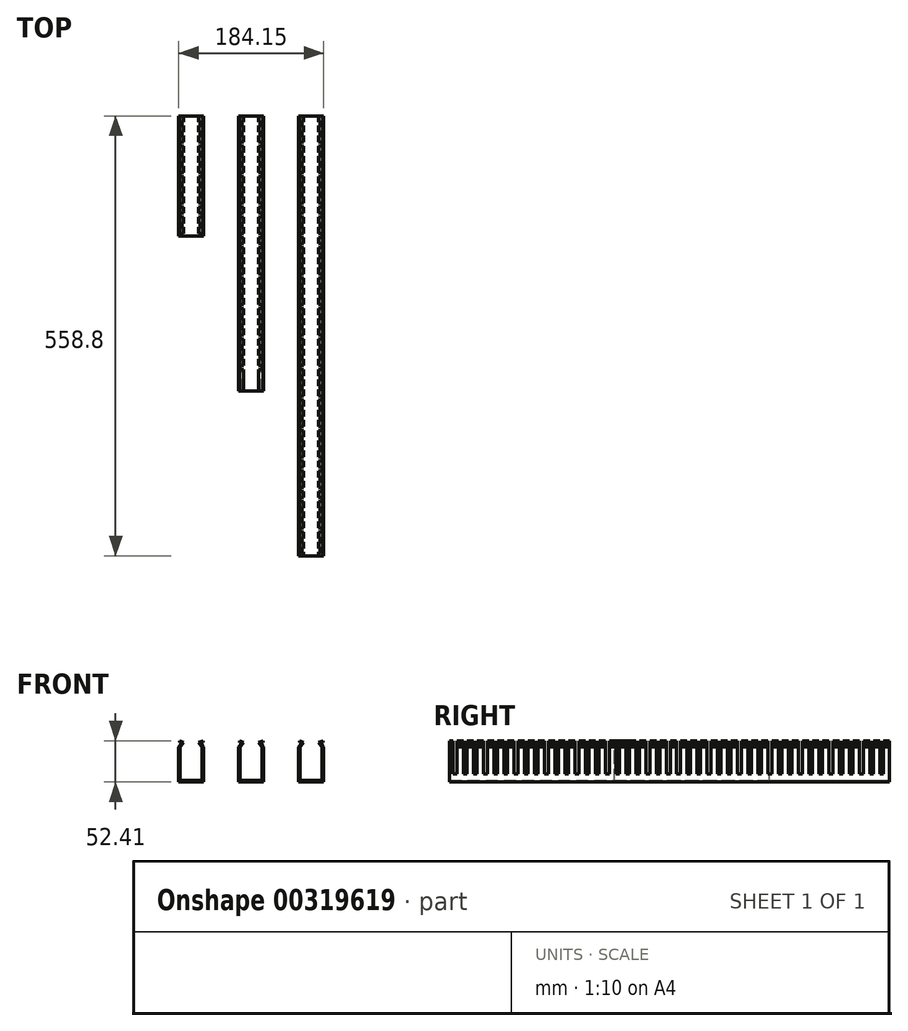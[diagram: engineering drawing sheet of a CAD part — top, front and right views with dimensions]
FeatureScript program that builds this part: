
annotation { "Feature Type Name" : "Feature", "Feature Type Description" : "" }
export const myFeature = defineFeature(function(context is Context, id is Id, definition is map)
    precondition{}
    {
        {
            var Q0;
            Q0=qCreatedBy(makeId("Front.planeOp"),FACE);
            var sketch = newSketch(context, id + "F0", { "sketchPlane" : qUnion([Q0])});
            skLineSegment(sketch, "E0", {"start": v(0, 0) * mm, "end": v(31.75, 0) * mm});
            skLineSegment(sketch, "E1", {"start": v(31.75, 0) * mm, "end": v(31.75, 44.45) * mm});
            skLineSegment(sketch, "E2", {"start": v(31.75, 44.45) * mm, "end": v(28.4, 49.24) * mm});
            skLineSegment(sketch, "E3", {"start": v(28.4, 49.24) * mm, "end": v(30.7, 50.3) * mm});
            skLineSegment(sketch, "E4", {"start": v(15.88, 0) * mm, "end": v(15.88, 8.95) * mm, "construction": true});
            skLineSegment(sketch, "E5.MirrorCS", {"start": v(0, 0) * mm, "end": v(0, 44.45) * mm});
            skLineSegment(sketch, "E6.MirrorCS", {"start": v(0, 44.45) * mm, "end": v(3.35, 49.24) * mm});
            skLineSegment(sketch, "E7.MirrorCS", {"start": v(3.35, 49.24) * mm, "end": v(1.05, 50.3) * mm});
            skLineSegment(sketch, "E8.0", {"start": v(25.54, 50) * mm, "end": v(30.7, 52.41) * mm});
            skLineSegment(sketch, "E8.1", {"start": v(29.84, 43.85) * mm, "end": v(25.54, 50) * mm});
            skLineSegment(sketch, "E8.2", {"start": v(29.85, 1.9) * mm, "end": v(29.85, 43.85) * mm});
            skLineSegment(sketch, "E8.3", {"start": v(6.21, 50) * mm, "end": v(1.05, 52.41) * mm});
            skLineSegment(sketch, "E8.4", {"start": v(1.9, 43.85) * mm, "end": v(6.21, 50) * mm});
            skLineSegment(sketch, "E8.5", {"start": v(1.9, 1.9) * mm, "end": v(1.9, 43.85) * mm});
            skLineSegment(sketch, "E8.6", {"start": v(1.9, 1.9) * mm, "end": v(29.85, 1.9) * mm});
            skLineSegment(sketch, "E9", {"start": v(30.7, 50.3) * mm, "end": v(30.7, 52.41) * mm});
            skLineSegment(sketch, "E10", {"start": v(1.05, 50.3) * mm, "end": v(1.05, 52.41) * mm});
            skLineSegment(sketch, "E11.1.0.0", {"start": v(-76.2, 0) * mm, "end": v(-44.45, 0) * mm});
            skLineSegment(sketch, "E11.1.0.1", {"start": v(-44.45, 0) * mm, "end": v(-44.45, 44.45) * mm});
            skLineSegment(sketch, "E11.1.0.2", {"start": v(-60.33, 0) * mm, "end": v(-60.33, 8.95) * mm, "construction": true});
            skLineSegment(sketch, "E11.1.0.3", {"start": v(-76.2, 0) * mm, "end": v(-76.2, 44.45) * mm});
            skLineSegment(sketch, "E11.1.0.4", {"start": v(-46.35, 1.9) * mm, "end": v(-46.35, 43.85) * mm});
            skLineSegment(sketch, "E11.1.0.5", {"start": v(-74.3, 1.9) * mm, "end": v(-74.3, 43.85) * mm});
            skLineSegment(sketch, "E11.1.0.6", {"start": v(-74.3, 1.9) * mm, "end": v(-46.35, 1.9) * mm});
            skLineSegment(sketch, "E11.1.0.7", {"start": v(-76.2, 44.45) * mm, "end": v(-72.85, 49.24) * mm});
            skLineSegment(sketch, "E11.1.0.8", {"start": v(-72.85, 49.24) * mm, "end": v(-75.15, 50.3) * mm});
            skLineSegment(sketch, "E11.1.0.9", {"start": v(-50.66, 50) * mm, "end": v(-45.5, 52.41) * mm});
            skLineSegment(sketch, "E11.1.0.10", {"start": v(-46.36, 43.85) * mm, "end": v(-50.66, 50) * mm});
            skLineSegment(sketch, "E11.1.0.11", {"start": v(-69.99, 50) * mm, "end": v(-75.15, 52.41) * mm});
            skLineSegment(sketch, "E11.1.0.12", {"start": v(-74.3, 43.85) * mm, "end": v(-69.99, 50) * mm});
            skLineSegment(sketch, "E11.1.0.13", {"start": v(-75.15, 50.3) * mm, "end": v(-75.15, 52.41) * mm});
            skLineSegment(sketch, "E11.1.0.14", {"start": v(-45.5, 50.3) * mm, "end": v(-45.5, 52.41) * mm});
            skLineSegment(sketch, "E11.1.0.15", {"start": v(-44.45, 44.45) * mm, "end": v(-47.8, 49.24) * mm});
            skLineSegment(sketch, "E11.1.0.16", {"start": v(-47.8, 49.24) * mm, "end": v(-45.5, 50.3) * mm});
            skLineSegment(sketch, "E11.2.0.0", {"start": v(-152.4, 0) * mm, "end": v(-120.65, 0) * mm});
            skLineSegment(sketch, "E11.2.0.1", {"start": v(-120.65, 0) * mm, "end": v(-120.65, 44.45) * mm});
            skLineSegment(sketch, "E11.2.0.2", {"start": v(-136.53, 0) * mm, "end": v(-136.53, 8.95) * mm, "construction": true});
            skLineSegment(sketch, "E11.2.0.3", {"start": v(-152.4, 0) * mm, "end": v(-152.4, 44.45) * mm});
            skLineSegment(sketch, "E11.2.0.4", {"start": v(-122.55, 1.9) * mm, "end": v(-122.55, 43.85) * mm});
            skLineSegment(sketch, "E11.2.0.5", {"start": v(-150.5, 1.9) * mm, "end": v(-150.5, 43.85) * mm});
            skLineSegment(sketch, "E11.2.0.6", {"start": v(-150.5, 1.9) * mm, "end": v(-122.55, 1.9) * mm});
            skLineSegment(sketch, "E11.2.0.7", {"start": v(-152.4, 44.45) * mm, "end": v(-149.05, 49.24) * mm});
            skLineSegment(sketch, "E11.2.0.8", {"start": v(-149.05, 49.24) * mm, "end": v(-151.35, 50.3) * mm});
            skLineSegment(sketch, "E11.2.0.9", {"start": v(-126.86, 50) * mm, "end": v(-121.7, 52.41) * mm});
            skLineSegment(sketch, "E11.2.0.10", {"start": v(-122.56, 43.85) * mm, "end": v(-126.86, 50) * mm});
            skLineSegment(sketch, "E11.2.0.11", {"start": v(-146.19, 50) * mm, "end": v(-151.35, 52.41) * mm});
            skLineSegment(sketch, "E11.2.0.12", {"start": v(-150.5, 43.85) * mm, "end": v(-146.19, 50) * mm});
            skLineSegment(sketch, "E11.2.0.13", {"start": v(-151.35, 50.3) * mm, "end": v(-151.35, 52.41) * mm});
            skLineSegment(sketch, "E11.2.0.14", {"start": v(-121.7, 50.3) * mm, "end": v(-121.7, 52.41) * mm});
            skLineSegment(sketch, "E11.2.0.15", {"start": v(-120.65, 44.45) * mm, "end": v(-124, 49.24) * mm});
            skLineSegment(sketch, "E11.2.0.16", {"start": v(-124, 49.24) * mm, "end": v(-121.7, 50.3) * mm});
            skLineSegment(sketch, "E11.direction1", {"start": v(0, 0) * mm, "end": v(-76.2, 0) * mm, "construction": true});
            skSolve(sketch);
        }
        {
            var Q0;
            Q0=makeQuery(id+"F0.imprint","IMPRINT",FACE,{"disambiguationData":[TD([[makeQuery(id+"F0.imprint","IMPRINT",EDGE,{"derivedFrom":sQuery(id+"F0.wireOp",EDGE,"E0")}),1.0]])]});
            extrude(context, id + "F1", {"entities" : qUnion([Q0]), "depth" : 558.8 * mm});
        }
        {
            var Q0;
            Q0=makeQuery(id+"F1.opExtrude","SWEPT_FACE",FACE,{"disambiguationData":[OSD([sQuery(id+"F0.wireOp",EDGE,"E1")])]});
            var sketch = newSketch(context, id + "F2", { "sketchPlane" : qUnion([Q0])});
            skLineSegment(sketch, "E12.0", {"start": v(-558.8, 0) * mm, "end": v(0, 0) * mm});
            skLineSegment(sketch, "E13.0", {"start": v(0, 0) * mm, "end": v(0, 44.45) * mm});
            skLineSegment(sketch, "E14.0", {"start": v(-7.62, 10.16) * mm, "end": v(-7.62, 52.41) * mm});
            skLineSegment(sketch, "E15.0", {"start": v(-12.32, 10.16) * mm, "end": v(-12.32, 52.41) * mm});
            skLineSegment(sketch, "E16.0", {"start": v(-12.32, 10.16) * mm, "end": v(-7.62, 10.16) * mm});
            skLineSegment(sketch, "E17.0", {"start": v(-12.32, 52.41) * mm, "end": v(-7.62, 52.41) * mm});
            skPoint(sketch, "E18.orphan", {"position": v(-558.8, 52.41) * mm});
            skLineSegment(sketch, "E19.1.0.0", {"start": v(-25.22, 10.16) * mm, "end": v(-25.22, 52.41) * mm});
            skLineSegment(sketch, "E19.1.0.1", {"start": v(-25.22, 10.16) * mm, "end": v(-20.52, 10.16) * mm});
            skLineSegment(sketch, "E19.1.0.2", {"start": v(-20.52, 10.16) * mm, "end": v(-20.52, 52.41) * mm});
            skLineSegment(sketch, "E19.1.0.3", {"start": v(-25.22, 52.41) * mm, "end": v(-20.52, 52.41) * mm});
            skLineSegment(sketch, "E19.2.0.0", {"start": v(-38.13, 10.16) * mm, "end": v(-38.13, 52.41) * mm});
            skLineSegment(sketch, "E19.2.0.1", {"start": v(-38.13, 10.16) * mm, "end": v(-33.43, 10.16) * mm});
            skLineSegment(sketch, "E19.2.0.2", {"start": v(-33.43, 10.16) * mm, "end": v(-33.43, 52.41) * mm});
            skLineSegment(sketch, "E19.2.0.3", {"start": v(-38.13, 52.41) * mm, "end": v(-33.43, 52.41) * mm});
            skLineSegment(sketch, "E19.3.0.0", {"start": v(-51.03, 10.16) * mm, "end": v(-51.03, 52.41) * mm});
            skLineSegment(sketch, "E19.3.0.1", {"start": v(-51.03, 10.16) * mm, "end": v(-46.33, 10.16) * mm});
            skLineSegment(sketch, "E19.3.0.2", {"start": v(-46.33, 10.16) * mm, "end": v(-46.33, 52.41) * mm});
            skLineSegment(sketch, "E19.3.0.3", {"start": v(-51.03, 52.41) * mm, "end": v(-46.33, 52.41) * mm});
            skLineSegment(sketch, "E19.4.0.0", {"start": v(-63.93, 10.16) * mm, "end": v(-63.93, 52.41) * mm});
            skLineSegment(sketch, "E19.4.0.1", {"start": v(-63.93, 10.16) * mm, "end": v(-59.23, 10.16) * mm});
            skLineSegment(sketch, "E19.4.0.2", {"start": v(-59.23, 10.16) * mm, "end": v(-59.23, 52.41) * mm});
            skLineSegment(sketch, "E19.4.0.3", {"start": v(-63.93, 52.41) * mm, "end": v(-59.23, 52.41) * mm});
            skLineSegment(sketch, "E19.5.0.0", {"start": v(-76.83, 10.16) * mm, "end": v(-76.83, 52.41) * mm});
            skLineSegment(sketch, "E19.5.0.1", {"start": v(-76.84, 10.16) * mm, "end": v(-72.14, 10.16) * mm});
            skLineSegment(sketch, "E19.5.0.2", {"start": v(-72.14, 10.16) * mm, "end": v(-72.14, 52.41) * mm});
            skLineSegment(sketch, "E19.5.0.3", {"start": v(-76.84, 52.41) * mm, "end": v(-72.14, 52.41) * mm});
            skLineSegment(sketch, "E19.6.0.0", {"start": v(-89.74, 10.16) * mm, "end": v(-89.74, 52.41) * mm});
            skLineSegment(sketch, "E19.6.0.1", {"start": v(-89.74, 10.16) * mm, "end": v(-85.04, 10.16) * mm});
            skLineSegment(sketch, "E19.6.0.2", {"start": v(-85.04, 10.16) * mm, "end": v(-85.04, 52.41) * mm});
            skLineSegment(sketch, "E19.6.0.3", {"start": v(-89.74, 52.41) * mm, "end": v(-85.04, 52.41) * mm});
            skLineSegment(sketch, "E19.7.0.0", {"start": v(-102.64, 10.16) * mm, "end": v(-102.64, 52.41) * mm});
            skLineSegment(sketch, "E19.7.0.1", {"start": v(-102.64, 10.16) * mm, "end": v(-97.94, 10.16) * mm});
            skLineSegment(sketch, "E19.7.0.2", {"start": v(-97.94, 10.16) * mm, "end": v(-97.94, 52.41) * mm});
            skLineSegment(sketch, "E19.7.0.3", {"start": v(-102.64, 52.41) * mm, "end": v(-97.94, 52.41) * mm});
            skLineSegment(sketch, "E19.8.0.0", {"start": v(-115.54, 10.16) * mm, "end": v(-115.54, 52.41) * mm});
            skLineSegment(sketch, "E19.8.0.1", {"start": v(-115.54, 10.16) * mm, "end": v(-110.85, 10.16) * mm});
            skLineSegment(sketch, "E19.8.0.2", {"start": v(-110.85, 10.16) * mm, "end": v(-110.85, 52.41) * mm});
            skLineSegment(sketch, "E19.8.0.3", {"start": v(-115.54, 52.41) * mm, "end": v(-110.85, 52.41) * mm});
            skLineSegment(sketch, "E19.9.0.0", {"start": v(-128.45, 10.16) * mm, "end": v(-128.45, 52.41) * mm});
            skLineSegment(sketch, "E19.9.0.1", {"start": v(-128.45, 10.16) * mm, "end": v(-123.75, 10.16) * mm});
            skLineSegment(sketch, "E19.9.0.2", {"start": v(-123.75, 10.16) * mm, "end": v(-123.75, 52.41) * mm});
            skLineSegment(sketch, "E19.9.0.3", {"start": v(-128.45, 52.41) * mm, "end": v(-123.75, 52.41) * mm});
            skLineSegment(sketch, "E19.10.0.0", {"start": v(-141.35, 10.16) * mm, "end": v(-141.35, 52.41) * mm});
            skLineSegment(sketch, "E19.10.0.1", {"start": v(-141.35, 10.16) * mm, "end": v(-136.65, 10.16) * mm});
            skLineSegment(sketch, "E19.10.0.2", {"start": v(-136.65, 10.16) * mm, "end": v(-136.65, 52.41) * mm});
            skLineSegment(sketch, "E19.10.0.3", {"start": v(-141.35, 52.41) * mm, "end": v(-136.65, 52.41) * mm});
            skLineSegment(sketch, "E19.11.0.0", {"start": v(-154.25, 10.16) * mm, "end": v(-154.25, 52.41) * mm});
            skLineSegment(sketch, "E19.11.0.1", {"start": v(-154.25, 10.16) * mm, "end": v(-149.56, 10.16) * mm});
            skLineSegment(sketch, "E19.11.0.2", {"start": v(-149.56, 10.16) * mm, "end": v(-149.56, 52.41) * mm});
            skLineSegment(sketch, "E19.11.0.3", {"start": v(-154.25, 52.41) * mm, "end": v(-149.56, 52.41) * mm});
            skLineSegment(sketch, "E19.12.0.0", {"start": v(-167.16, 10.16) * mm, "end": v(-167.16, 52.41) * mm});
            skLineSegment(sketch, "E19.12.0.1", {"start": v(-167.16, 10.16) * mm, "end": v(-162.46, 10.16) * mm});
            skLineSegment(sketch, "E19.12.0.2", {"start": v(-162.46, 10.16) * mm, "end": v(-162.46, 52.41) * mm});
            skLineSegment(sketch, "E19.12.0.3", {"start": v(-167.16, 52.41) * mm, "end": v(-162.46, 52.41) * mm});
            skLineSegment(sketch, "E19.13.0.0", {"start": v(-180.06, 10.16) * mm, "end": v(-180.06, 52.41) * mm});
            skLineSegment(sketch, "E19.13.0.1", {"start": v(-180.06, 10.16) * mm, "end": v(-175.36, 10.16) * mm});
            skLineSegment(sketch, "E19.13.0.2", {"start": v(-175.36, 10.16) * mm, "end": v(-175.36, 52.41) * mm});
            skLineSegment(sketch, "E19.13.0.3", {"start": v(-180.06, 52.41) * mm, "end": v(-175.36, 52.41) * mm});
            skLineSegment(sketch, "E19.14.0.0", {"start": v(-192.96, 10.16) * mm, "end": v(-192.96, 52.41) * mm});
            skLineSegment(sketch, "E19.14.0.1", {"start": v(-192.96, 10.16) * mm, "end": v(-188.26, 10.16) * mm});
            skLineSegment(sketch, "E19.14.0.2", {"start": v(-188.26, 10.16) * mm, "end": v(-188.26, 52.41) * mm});
            skLineSegment(sketch, "E19.14.0.3", {"start": v(-192.96, 52.41) * mm, "end": v(-188.26, 52.41) * mm});
            skLineSegment(sketch, "E19.15.0.0", {"start": v(-205.87, 10.16) * mm, "end": v(-205.87, 52.41) * mm});
            skLineSegment(sketch, "E19.15.0.1", {"start": v(-205.87, 10.16) * mm, "end": v(-201.17, 10.16) * mm});
            skLineSegment(sketch, "E19.15.0.2", {"start": v(-201.17, 10.16) * mm, "end": v(-201.17, 52.41) * mm});
            skLineSegment(sketch, "E19.15.0.3", {"start": v(-205.87, 52.41) * mm, "end": v(-201.17, 52.41) * mm});
            skLineSegment(sketch, "E19.16.0.0", {"start": v(-218.77, 10.16) * mm, "end": v(-218.77, 52.41) * mm});
            skLineSegment(sketch, "E19.16.0.1", {"start": v(-218.77, 10.16) * mm, "end": v(-214.07, 10.16) * mm});
            skLineSegment(sketch, "E19.16.0.2", {"start": v(-214.07, 10.16) * mm, "end": v(-214.07, 52.41) * mm});
            skLineSegment(sketch, "E19.16.0.3", {"start": v(-218.77, 52.41) * mm, "end": v(-214.07, 52.41) * mm});
            skLineSegment(sketch, "E19.17.0.0", {"start": v(-231.67, 10.16) * mm, "end": v(-231.67, 52.41) * mm});
            skLineSegment(sketch, "E19.17.0.1", {"start": v(-231.67, 10.16) * mm, "end": v(-226.97, 10.16) * mm});
            skLineSegment(sketch, "E19.17.0.2", {"start": v(-226.97, 10.16) * mm, "end": v(-226.97, 52.41) * mm});
            skLineSegment(sketch, "E19.17.0.3", {"start": v(-231.67, 52.41) * mm, "end": v(-226.97, 52.41) * mm});
            skLineSegment(sketch, "E19.18.0.0", {"start": v(-244.58, 10.16) * mm, "end": v(-244.58, 52.41) * mm});
            skLineSegment(sketch, "E19.18.0.1", {"start": v(-244.58, 10.16) * mm, "end": v(-239.88, 10.16) * mm});
            skLineSegment(sketch, "E19.18.0.2", {"start": v(-239.88, 10.16) * mm, "end": v(-239.88, 52.41) * mm});
            skLineSegment(sketch, "E19.18.0.3", {"start": v(-244.58, 52.41) * mm, "end": v(-239.88, 52.41) * mm});
            skLineSegment(sketch, "E19.19.0.0", {"start": v(-257.48, 10.16) * mm, "end": v(-257.48, 52.41) * mm});
            skLineSegment(sketch, "E19.19.0.1", {"start": v(-257.48, 10.16) * mm, "end": v(-252.78, 10.16) * mm});
            skLineSegment(sketch, "E19.19.0.2", {"start": v(-252.78, 10.16) * mm, "end": v(-252.78, 52.41) * mm});
            skLineSegment(sketch, "E19.19.0.3", {"start": v(-257.48, 52.41) * mm, "end": v(-252.78, 52.41) * mm});
            skLineSegment(sketch, "E19.direction1", {"start": v(-12.32, 10.16) * mm, "end": v(-25.22, 10.16) * mm, "construction": true});
            skLineSegment(sketch, "E20.0.20.0", {"start": v(-270.38, 10.16) * mm, "end": v(-270.38, 52.41) * mm});
            skLineSegment(sketch, "E20.3.20.0", {"start": v(-270.38, 10.16) * mm, "end": v(-265.68, 10.16) * mm});
            skLineSegment(sketch, "E20.6.20.0", {"start": v(-265.68, 10.16) * mm, "end": v(-265.68, 52.41) * mm});
            skLineSegment(sketch, "E20.9.20.0", {"start": v(-270.38, 52.41) * mm, "end": v(-265.68, 52.41) * mm});
            skLineSegment(sketch, "E20.0.21.0", {"start": v(-283.29, 10.16) * mm, "end": v(-283.29, 52.41) * mm});
            skLineSegment(sketch, "E20.3.21.0", {"start": v(-283.29, 10.16) * mm, "end": v(-278.59, 10.16) * mm});
            skLineSegment(sketch, "E20.6.21.0", {"start": v(-278.59, 10.16) * mm, "end": v(-278.59, 52.41) * mm});
            skLineSegment(sketch, "E20.9.21.0", {"start": v(-283.29, 52.41) * mm, "end": v(-278.59, 52.41) * mm});
            skLineSegment(sketch, "E20.0.22.0", {"start": v(-296.19, 10.16) * mm, "end": v(-296.19, 52.41) * mm});
            skLineSegment(sketch, "E20.3.22.0", {"start": v(-296.19, 10.16) * mm, "end": v(-291.5, 10.16) * mm});
            skLineSegment(sketch, "E20.6.22.0", {"start": v(-291.5, 10.16) * mm, "end": v(-291.5, 52.41) * mm});
            skLineSegment(sketch, "E20.9.22.0", {"start": v(-296.19, 52.41) * mm, "end": v(-291.5, 52.41) * mm});
            skLineSegment(sketch, "E20.0.23.0", {"start": v(-309.1, 10.16) * mm, "end": v(-309.1, 52.41) * mm});
            skLineSegment(sketch, "E20.3.23.0", {"start": v(-309.1, 10.16) * mm, "end": v(-304.4, 10.16) * mm});
            skLineSegment(sketch, "E20.6.23.0", {"start": v(-304.4, 10.16) * mm, "end": v(-304.4, 52.41) * mm});
            skLineSegment(sketch, "E20.9.23.0", {"start": v(-309.1, 52.41) * mm, "end": v(-304.4, 52.41) * mm});
            skLineSegment(sketch, "E20.0.24.0", {"start": v(-322, 10.16) * mm, "end": v(-322, 52.41) * mm});
            skLineSegment(sketch, "E20.3.24.0", {"start": v(-322, 10.16) * mm, "end": v(-317.3, 10.16) * mm});
            skLineSegment(sketch, "E20.6.24.0", {"start": v(-317.3, 10.16) * mm, "end": v(-317.3, 52.41) * mm});
            skLineSegment(sketch, "E20.9.24.0", {"start": v(-322, 52.41) * mm, "end": v(-317.3, 52.41) * mm});
            skLineSegment(sketch, "E20.0.25.0", {"start": v(-334.9, 10.16) * mm, "end": v(-334.9, 52.41) * mm});
            skLineSegment(sketch, "E20.3.25.0", {"start": v(-334.9, 10.16) * mm, "end": v(-330.2, 10.16) * mm});
            skLineSegment(sketch, "E20.6.25.0", {"start": v(-330.2, 10.16) * mm, "end": v(-330.2, 52.41) * mm});
            skLineSegment(sketch, "E20.9.25.0", {"start": v(-334.9, 52.41) * mm, "end": v(-330.2, 52.41) * mm});
            skLineSegment(sketch, "E20.0.26.0", {"start": v(-347.8, 10.16) * mm, "end": v(-347.8, 52.41) * mm});
            skLineSegment(sketch, "E20.3.26.0", {"start": v(-347.8, 10.16) * mm, "end": v(-343.1, 10.16) * mm});
            skLineSegment(sketch, "E20.6.26.0", {"start": v(-343.1, 10.16) * mm, "end": v(-343.1, 52.41) * mm});
            skLineSegment(sketch, "E20.9.26.0", {"start": v(-347.8, 52.41) * mm, "end": v(-343.1, 52.41) * mm});
            skLineSegment(sketch, "E20.0.27.0", {"start": v(-360.7, 10.16) * mm, "end": v(-360.7, 52.41) * mm});
            skLineSegment(sketch, "E20.3.27.0", {"start": v(-360.7, 10.16) * mm, "end": v(-356, 10.16) * mm});
            skLineSegment(sketch, "E20.6.27.0", {"start": v(-356, 10.16) * mm, "end": v(-356, 52.41) * mm});
            skLineSegment(sketch, "E20.9.27.0", {"start": v(-360.7, 52.41) * mm, "end": v(-356, 52.41) * mm});
            skLineSegment(sketch, "E20.0.28.0", {"start": v(-373.6, 10.16) * mm, "end": v(-373.6, 52.41) * mm});
            skLineSegment(sketch, "E20.3.28.0", {"start": v(-373.6, 10.16) * mm, "end": v(-368.9, 10.16) * mm});
            skLineSegment(sketch, "E20.6.28.0", {"start": v(-368.9, 10.16) * mm, "end": v(-368.9, 52.41) * mm});
            skLineSegment(sketch, "E20.9.28.0", {"start": v(-373.6, 52.41) * mm, "end": v(-368.9, 52.41) * mm});
            skLineSegment(sketch, "E20.0.29.0", {"start": v(-386.51, 10.16) * mm, "end": v(-386.51, 52.41) * mm});
            skLineSegment(sketch, "E20.3.29.0", {"start": v(-386.51, 10.16) * mm, "end": v(-381.81, 10.16) * mm});
            skLineSegment(sketch, "E20.6.29.0", {"start": v(-381.81, 10.16) * mm, "end": v(-381.81, 52.41) * mm});
            skLineSegment(sketch, "E20.9.29.0", {"start": v(-386.51, 52.41) * mm, "end": v(-381.81, 52.41) * mm});
            skLineSegment(sketch, "E21.0.30.0", {"start": v(-399.42, 10.16) * mm, "end": v(-399.42, 52.41) * mm});
            skLineSegment(sketch, "E21.3.30.0", {"start": v(-399.42, 10.16) * mm, "end": v(-394.72, 10.16) * mm});
            skLineSegment(sketch, "E21.6.30.0", {"start": v(-394.72, 10.16) * mm, "end": v(-394.72, 52.41) * mm});
            skLineSegment(sketch, "E21.9.30.0", {"start": v(-399.42, 52.41) * mm, "end": v(-394.72, 52.41) * mm});
            skLineSegment(sketch, "E21.0.31.0", {"start": v(-412.32, 10.16) * mm, "end": v(-412.32, 52.41) * mm});
            skLineSegment(sketch, "E21.3.31.0", {"start": v(-412.32, 10.16) * mm, "end": v(-407.62, 10.16) * mm});
            skLineSegment(sketch, "E21.6.31.0", {"start": v(-407.62, 10.16) * mm, "end": v(-407.62, 52.41) * mm});
            skLineSegment(sketch, "E21.9.31.0", {"start": v(-412.32, 52.41) * mm, "end": v(-407.62, 52.41) * mm});
            skLineSegment(sketch, "E21.0.32.0", {"start": v(-425.22, 10.16) * mm, "end": v(-425.22, 52.41) * mm});
            skLineSegment(sketch, "E21.3.32.0", {"start": v(-425.22, 10.16) * mm, "end": v(-420.52, 10.16) * mm});
            skLineSegment(sketch, "E21.6.32.0", {"start": v(-420.52, 10.16) * mm, "end": v(-420.52, 52.41) * mm});
            skLineSegment(sketch, "E21.9.32.0", {"start": v(-425.22, 52.41) * mm, "end": v(-420.52, 52.41) * mm});
            skLineSegment(sketch, "E21.0.33.0", {"start": v(-438.12, 10.16) * mm, "end": v(-438.12, 52.41) * mm});
            skLineSegment(sketch, "E21.3.33.0", {"start": v(-438.12, 10.16) * mm, "end": v(-433.43, 10.16) * mm});
            skLineSegment(sketch, "E21.6.33.0", {"start": v(-433.43, 10.16) * mm, "end": v(-433.43, 52.41) * mm});
            skLineSegment(sketch, "E21.9.33.0", {"start": v(-438.12, 52.41) * mm, "end": v(-433.43, 52.41) * mm});
            skLineSegment(sketch, "E21.0.34.0", {"start": v(-451.03, 10.16) * mm, "end": v(-451.03, 52.41) * mm});
            skLineSegment(sketch, "E21.3.34.0", {"start": v(-451.03, 10.16) * mm, "end": v(-446.33, 10.16) * mm});
            skLineSegment(sketch, "E21.6.34.0", {"start": v(-446.33, 10.16) * mm, "end": v(-446.33, 52.41) * mm});
            skLineSegment(sketch, "E21.9.34.0", {"start": v(-451.03, 52.41) * mm, "end": v(-446.33, 52.41) * mm});
            skLineSegment(sketch, "E21.0.35.0", {"start": v(-463.93, 10.16) * mm, "end": v(-463.93, 52.41) * mm});
            skLineSegment(sketch, "E21.3.35.0", {"start": v(-463.93, 10.16) * mm, "end": v(-459.23, 10.16) * mm});
            skLineSegment(sketch, "E21.6.35.0", {"start": v(-459.23, 10.16) * mm, "end": v(-459.23, 52.41) * mm});
            skLineSegment(sketch, "E21.9.35.0", {"start": v(-463.93, 52.41) * mm, "end": v(-459.23, 52.41) * mm});
            skLineSegment(sketch, "E21.0.36.0", {"start": v(-476.83, 10.16) * mm, "end": v(-476.83, 52.41) * mm});
            skLineSegment(sketch, "E21.3.36.0", {"start": v(-476.83, 10.16) * mm, "end": v(-472.14, 10.16) * mm});
            skLineSegment(sketch, "E21.6.36.0", {"start": v(-472.14, 10.16) * mm, "end": v(-472.14, 52.41) * mm});
            skLineSegment(sketch, "E21.9.36.0", {"start": v(-476.83, 52.41) * mm, "end": v(-472.14, 52.41) * mm});
            skLineSegment(sketch, "E21.0.37.0", {"start": v(-489.74, 10.16) * mm, "end": v(-489.74, 52.41) * mm});
            skLineSegment(sketch, "E21.3.37.0", {"start": v(-489.74, 10.16) * mm, "end": v(-485.04, 10.16) * mm});
            skLineSegment(sketch, "E21.6.37.0", {"start": v(-485.04, 10.16) * mm, "end": v(-485.04, 52.41) * mm});
            skLineSegment(sketch, "E21.9.37.0", {"start": v(-489.74, 52.41) * mm, "end": v(-485.04, 52.41) * mm});
            skLineSegment(sketch, "E21.0.38.0", {"start": v(-502.64, 10.16) * mm, "end": v(-502.64, 52.41) * mm});
            skLineSegment(sketch, "E21.3.38.0", {"start": v(-502.64, 10.16) * mm, "end": v(-497.94, 10.16) * mm});
            skLineSegment(sketch, "E21.6.38.0", {"start": v(-497.94, 10.16) * mm, "end": v(-497.94, 52.41) * mm});
            skLineSegment(sketch, "E21.9.38.0", {"start": v(-502.64, 52.41) * mm, "end": v(-497.94, 52.41) * mm});
            skLineSegment(sketch, "E21.0.39.0", {"start": v(-515.54, 10.16) * mm, "end": v(-515.54, 52.41) * mm});
            skLineSegment(sketch, "E21.3.39.0", {"start": v(-515.54, 10.16) * mm, "end": v(-510.84, 10.16) * mm});
            skLineSegment(sketch, "E21.6.39.0", {"start": v(-510.84, 10.16) * mm, "end": v(-510.84, 52.41) * mm});
            skLineSegment(sketch, "E21.9.39.0", {"start": v(-515.54, 52.41) * mm, "end": v(-510.84, 52.41) * mm});
            skLineSegment(sketch, "E22.0.40.0", {"start": v(-528.45, 10.16) * mm, "end": v(-528.45, 52.41) * mm});
            skLineSegment(sketch, "E22.3.40.0", {"start": v(-528.45, 10.16) * mm, "end": v(-523.75, 10.16) * mm});
            skLineSegment(sketch, "E22.6.40.0", {"start": v(-523.75, 10.16) * mm, "end": v(-523.75, 52.41) * mm});
            skLineSegment(sketch, "E22.9.40.0", {"start": v(-528.45, 52.41) * mm, "end": v(-523.75, 52.41) * mm});
            skLineSegment(sketch, "E22.0.41.0", {"start": v(-541.35, 10.16) * mm, "end": v(-541.35, 52.41) * mm});
            skLineSegment(sketch, "E22.3.41.0", {"start": v(-541.35, 10.16) * mm, "end": v(-536.65, 10.16) * mm});
            skLineSegment(sketch, "E22.6.41.0", {"start": v(-536.65, 10.16) * mm, "end": v(-536.65, 52.41) * mm});
            skLineSegment(sketch, "E22.9.41.0", {"start": v(-541.35, 52.41) * mm, "end": v(-536.65, 52.41) * mm});
            skLineSegment(sketch, "E22.0.42.0", {"start": v(-554.25, 10.16) * mm, "end": v(-554.25, 52.41) * mm});
            skLineSegment(sketch, "E22.3.42.0", {"start": v(-554.25, 10.16) * mm, "end": v(-549.55, 10.16) * mm});
            skLineSegment(sketch, "E22.6.42.0", {"start": v(-549.55, 10.16) * mm, "end": v(-549.55, 52.41) * mm});
            skLineSegment(sketch, "E22.9.42.0", {"start": v(-554.25, 52.41) * mm, "end": v(-549.55, 52.41) * mm});
            skLineSegment(sketch, "E22.0.43.0", {"start": v(-567.16, 10.16) * mm, "end": v(-567.16, 52.41) * mm});
            skLineSegment(sketch, "E22.3.43.0", {"start": v(-567.16, 10.16) * mm, "end": v(-562.46, 10.16) * mm});
            skLineSegment(sketch, "E22.6.43.0", {"start": v(-562.46, 10.16) * mm, "end": v(-562.46, 52.41) * mm});
            skLineSegment(sketch, "E22.9.43.0", {"start": v(-567.16, 52.41) * mm, "end": v(-562.46, 52.41) * mm});
            skLineSegment(sketch, "E22.0.44.0", {"start": v(-580.06, 10.16) * mm, "end": v(-580.06, 52.41) * mm});
            skLineSegment(sketch, "E22.3.44.0", {"start": v(-580.06, 10.16) * mm, "end": v(-575.36, 10.16) * mm});
            skLineSegment(sketch, "E22.6.44.0", {"start": v(-575.36, 10.16) * mm, "end": v(-575.36, 52.41) * mm});
            skLineSegment(sketch, "E22.9.44.0", {"start": v(-580.06, 52.41) * mm, "end": v(-575.36, 52.41) * mm});
            skSolve(sketch);
        }
        {
            var Q0;
            {var subQ0=sQuery(id+"F2.wireOp",EDGE,"E16.0");Q0=makeQuery(id+"F2.imprint","IMPRINT",FACE,{"disambiguationData":[TD([[makeQuery(id+"F2.imprint","IMPRINT",EDGE,{"derivedFrom":subQ0}),1.0]])]});}
            var Q1;
            {var subQ0=sQuery(id+"F2.wireOp",EDGE,"E17.0");Q1=makeQuery(id+"F2.imprint","IMPRINT",FACE,{"disambiguationData":[TD([[makeQuery(id+"F2.imprint","IMPRINT",EDGE,{"derivedFrom":subQ0}),-1.0]])]});}
            var Q2;
            {var subQ0=sQuery(id+"F2.wireOp",EDGE,"E19.1.0.3");Q2=makeQuery(id+"F2.imprint","IMPRINT",FACE,{"disambiguationData":[TD([[makeQuery(id+"F2.imprint","IMPRINT",EDGE,{"derivedFrom":subQ0}),-1.0]])]});}
            var Q3;
            {var subQ0=sQuery(id+"F2.wireOp",EDGE,"E19.1.0.1");Q3=makeQuery(id+"F2.imprint","IMPRINT",FACE,{"disambiguationData":[TD([[makeQuery(id+"F2.imprint","IMPRINT",EDGE,{"derivedFrom":subQ0}),1.0]])]});}
            var Q4;
            {var subQ0=sQuery(id+"F2.wireOp",EDGE,"E19.2.0.1");Q4=makeQuery(id+"F2.imprint","IMPRINT",FACE,{"disambiguationData":[TD([[makeQuery(id+"F2.imprint","IMPRINT",EDGE,{"derivedFrom":subQ0}),1.0]])]});}
            var Q5;
            {var subQ0=sQuery(id+"F2.wireOp",EDGE,"E19.2.0.3");Q5=makeQuery(id+"F2.imprint","IMPRINT",FACE,{"disambiguationData":[TD([[makeQuery(id+"F2.imprint","IMPRINT",EDGE,{"derivedFrom":subQ0}),-1.0]])]});}
            var Q6;
            {var subQ0=sQuery(id+"F2.wireOp",EDGE,"E19.3.0.3");Q6=makeQuery(id+"F2.imprint","IMPRINT",FACE,{"disambiguationData":[TD([[makeQuery(id+"F2.imprint","IMPRINT",EDGE,{"derivedFrom":subQ0}),-1.0]])]});}
            var Q7;
            {var subQ0=sQuery(id+"F2.wireOp",EDGE,"E19.3.0.1");Q7=makeQuery(id+"F2.imprint","IMPRINT",FACE,{"disambiguationData":[TD([[makeQuery(id+"F2.imprint","IMPRINT",EDGE,{"derivedFrom":subQ0}),1.0]])]});}
            var Q8;
            {var subQ0=sQuery(id+"F2.wireOp",EDGE,"E19.4.0.3");Q8=makeQuery(id+"F2.imprint","IMPRINT",FACE,{"disambiguationData":[TD([[makeQuery(id+"F2.imprint","IMPRINT",EDGE,{"derivedFrom":subQ0}),-1.0]])]});}
            var Q9;
            {var subQ0=sQuery(id+"F2.wireOp",EDGE,"E19.4.0.1");Q9=makeQuery(id+"F2.imprint","IMPRINT",FACE,{"disambiguationData":[TD([[makeQuery(id+"F2.imprint","IMPRINT",EDGE,{"derivedFrom":subQ0}),1.0]])]});}
            var Q10;
            {var subQ0=sQuery(id+"F2.wireOp",EDGE,"E19.5.0.1");Q10=makeQuery(id+"F2.imprint","IMPRINT",FACE,{"disambiguationData":[TD([[makeQuery(id+"F2.imprint","IMPRINT",EDGE,{"derivedFrom":subQ0}),1.0]])]});}
            var Q11;
            {var subQ0=sQuery(id+"F2.wireOp",EDGE,"E19.6.0.1");Q11=makeQuery(id+"F2.imprint","IMPRINT",FACE,{"disambiguationData":[TD([[makeQuery(id+"F2.imprint","IMPRINT",EDGE,{"derivedFrom":subQ0}),1.0]])]});}
            var Q12;
            {var subQ0=sQuery(id+"F2.wireOp",EDGE,"E19.7.0.1");Q12=makeQuery(id+"F2.imprint","IMPRINT",FACE,{"disambiguationData":[TD([[makeQuery(id+"F2.imprint","IMPRINT",EDGE,{"derivedFrom":subQ0}),1.0]])]});}
            var Q13;
            {var subQ0=sQuery(id+"F2.wireOp",EDGE,"E19.8.0.1");Q13=makeQuery(id+"F2.imprint","IMPRINT",FACE,{"disambiguationData":[TD([[makeQuery(id+"F2.imprint","IMPRINT",EDGE,{"derivedFrom":subQ0}),1.0]])]});}
            var Q14;
            {var subQ0=sQuery(id+"F2.wireOp",EDGE,"E19.8.0.3");Q14=makeQuery(id+"F2.imprint","IMPRINT",FACE,{"disambiguationData":[TD([[makeQuery(id+"F2.imprint","IMPRINT",EDGE,{"derivedFrom":subQ0}),-1.0]])]});}
            var Q15;
            {var subQ0=sQuery(id+"F2.wireOp",EDGE,"E19.7.0.3");Q15=makeQuery(id+"F2.imprint","IMPRINT",FACE,{"disambiguationData":[TD([[makeQuery(id+"F2.imprint","IMPRINT",EDGE,{"derivedFrom":subQ0}),-1.0]])]});}
            var Q16;
            {var subQ0=sQuery(id+"F2.wireOp",EDGE,"E19.6.0.3");Q16=makeQuery(id+"F2.imprint","IMPRINT",FACE,{"disambiguationData":[TD([[makeQuery(id+"F2.imprint","IMPRINT",EDGE,{"derivedFrom":subQ0}),-1.0]])]});}
            var Q17;
            {var subQ0=sQuery(id+"F2.wireOp",EDGE,"E19.5.0.3");Q17=makeQuery(id+"F2.imprint","IMPRINT",FACE,{"disambiguationData":[TD([[makeQuery(id+"F2.imprint","IMPRINT",EDGE,{"derivedFrom":subQ0}),-1.0]])]});}
            var Q18;
            {var subQ0=sQuery(id+"F2.wireOp",EDGE,"E19.9.0.3");Q18=makeQuery(id+"F2.imprint","IMPRINT",FACE,{"disambiguationData":[TD([[makeQuery(id+"F2.imprint","IMPRINT",EDGE,{"derivedFrom":subQ0}),-1.0]])]});}
            var Q19;
            {var subQ0=sQuery(id+"F2.wireOp",EDGE,"E19.9.0.1");Q19=makeQuery(id+"F2.imprint","IMPRINT",FACE,{"disambiguationData":[TD([[makeQuery(id+"F2.imprint","IMPRINT",EDGE,{"derivedFrom":subQ0}),1.0]])]});}
            var Q20;
            {var subQ0=sQuery(id+"F2.wireOp",EDGE,"E19.10.0.3");Q20=makeQuery(id+"F2.imprint","IMPRINT",FACE,{"disambiguationData":[TD([[makeQuery(id+"F2.imprint","IMPRINT",EDGE,{"derivedFrom":subQ0}),-1.0]])]});}
            var Q21;
            {var subQ0=sQuery(id+"F2.wireOp",EDGE,"E19.10.0.1");Q21=makeQuery(id+"F2.imprint","IMPRINT",FACE,{"disambiguationData":[TD([[makeQuery(id+"F2.imprint","IMPRINT",EDGE,{"derivedFrom":subQ0}),1.0]])]});}
            var Q22;
            {var subQ0=sQuery(id+"F2.wireOp",EDGE,"E19.11.0.3");Q22=makeQuery(id+"F2.imprint","IMPRINT",FACE,{"disambiguationData":[TD([[makeQuery(id+"F2.imprint","IMPRINT",EDGE,{"derivedFrom":subQ0}),-1.0]])]});}
            var Q23;
            {var subQ0=sQuery(id+"F2.wireOp",EDGE,"E19.11.0.1");Q23=makeQuery(id+"F2.imprint","IMPRINT",FACE,{"disambiguationData":[TD([[makeQuery(id+"F2.imprint","IMPRINT",EDGE,{"derivedFrom":subQ0}),1.0]])]});}
            var Q24;
            {var subQ0=sQuery(id+"F2.wireOp",EDGE,"E19.12.0.3");Q24=makeQuery(id+"F2.imprint","IMPRINT",FACE,{"disambiguationData":[TD([[makeQuery(id+"F2.imprint","IMPRINT",EDGE,{"derivedFrom":subQ0}),-1.0]])]});}
            var Q25;
            {var subQ0=sQuery(id+"F2.wireOp",EDGE,"E19.12.0.1");Q25=makeQuery(id+"F2.imprint","IMPRINT",FACE,{"disambiguationData":[TD([[makeQuery(id+"F2.imprint","IMPRINT",EDGE,{"derivedFrom":subQ0}),1.0]])]});}
            var Q26;
            {var subQ0=sQuery(id+"F2.wireOp",EDGE,"E19.13.0.3");Q26=makeQuery(id+"F2.imprint","IMPRINT",FACE,{"disambiguationData":[TD([[makeQuery(id+"F2.imprint","IMPRINT",EDGE,{"derivedFrom":subQ0}),-1.0]])]});}
            var Q27;
            {var subQ0=sQuery(id+"F2.wireOp",EDGE,"E19.13.0.1");Q27=makeQuery(id+"F2.imprint","IMPRINT",FACE,{"disambiguationData":[TD([[makeQuery(id+"F2.imprint","IMPRINT",EDGE,{"derivedFrom":subQ0}),1.0]])]});}
            var Q28;
            {var subQ0=sQuery(id+"F2.wireOp",EDGE,"E19.14.0.1");Q28=makeQuery(id+"F2.imprint","IMPRINT",FACE,{"disambiguationData":[TD([[makeQuery(id+"F2.imprint","IMPRINT",EDGE,{"derivedFrom":subQ0}),1.0]])]});}
            var Q29;
            {var subQ0=sQuery(id+"F2.wireOp",EDGE,"E19.14.0.3");Q29=makeQuery(id+"F2.imprint","IMPRINT",FACE,{"disambiguationData":[TD([[makeQuery(id+"F2.imprint","IMPRINT",EDGE,{"derivedFrom":subQ0}),-1.0]])]});}
            var Q30;
            {var subQ0=sQuery(id+"F2.wireOp",EDGE,"E19.15.0.3");Q30=makeQuery(id+"F2.imprint","IMPRINT",FACE,{"disambiguationData":[TD([[makeQuery(id+"F2.imprint","IMPRINT",EDGE,{"derivedFrom":subQ0}),-1.0]])]});}
            var Q31;
            {var subQ0=sQuery(id+"F2.wireOp",EDGE,"E19.15.0.1");Q31=makeQuery(id+"F2.imprint","IMPRINT",FACE,{"disambiguationData":[TD([[makeQuery(id+"F2.imprint","IMPRINT",EDGE,{"derivedFrom":subQ0}),1.0]])]});}
            var Q32;
            {var subQ0=sQuery(id+"F2.wireOp",EDGE,"E19.16.0.3");Q32=makeQuery(id+"F2.imprint","IMPRINT",FACE,{"disambiguationData":[TD([[makeQuery(id+"F2.imprint","IMPRINT",EDGE,{"derivedFrom":subQ0}),-1.0]])]});}
            var Q33;
            {var subQ0=sQuery(id+"F2.wireOp",EDGE,"E19.16.0.1");Q33=makeQuery(id+"F2.imprint","IMPRINT",FACE,{"disambiguationData":[TD([[makeQuery(id+"F2.imprint","IMPRINT",EDGE,{"derivedFrom":subQ0}),1.0]])]});}
            var Q34;
            {var subQ0=sQuery(id+"F2.wireOp",EDGE,"E19.17.0.3");Q34=makeQuery(id+"F2.imprint","IMPRINT",FACE,{"disambiguationData":[TD([[makeQuery(id+"F2.imprint","IMPRINT",EDGE,{"derivedFrom":subQ0}),-1.0]])]});}
            var Q35;
            {var subQ0=sQuery(id+"F2.wireOp",EDGE,"E19.17.0.1");Q35=makeQuery(id+"F2.imprint","IMPRINT",FACE,{"disambiguationData":[TD([[makeQuery(id+"F2.imprint","IMPRINT",EDGE,{"derivedFrom":subQ0}),1.0]])]});}
            var Q36;
            {var subQ0=sQuery(id+"F2.wireOp",EDGE,"E19.18.0.1");Q36=makeQuery(id+"F2.imprint","IMPRINT",FACE,{"disambiguationData":[TD([[makeQuery(id+"F2.imprint","IMPRINT",EDGE,{"derivedFrom":subQ0}),1.0]])]});}
            var Q37;
            {var subQ0=sQuery(id+"F2.wireOp",EDGE,"E19.18.0.3");Q37=makeQuery(id+"F2.imprint","IMPRINT",FACE,{"disambiguationData":[TD([[makeQuery(id+"F2.imprint","IMPRINT",EDGE,{"derivedFrom":subQ0}),-1.0]])]});}
            var Q38;
            {var subQ0=sQuery(id+"F2.wireOp",EDGE,"E19.19.0.1");Q38=makeQuery(id+"F2.imprint","IMPRINT",FACE,{"disambiguationData":[TD([[makeQuery(id+"F2.imprint","IMPRINT",EDGE,{"derivedFrom":subQ0}),1.0]])]});}
            var Q39;
            {var subQ0=sQuery(id+"F2.wireOp",EDGE,"E19.19.0.3");Q39=makeQuery(id+"F2.imprint","IMPRINT",FACE,{"disambiguationData":[TD([[makeQuery(id+"F2.imprint","IMPRINT",EDGE,{"derivedFrom":subQ0}),-1.0]])]});}
            var Q40;
            {var subQ0=sQuery(id+"F2.wireOp",EDGE,"E20.9.20.0");Q40=makeQuery(id+"F2.imprint","IMPRINT",FACE,{"disambiguationData":[TD([[makeQuery(id+"F2.imprint","IMPRINT",EDGE,{"derivedFrom":subQ0}),-1.0]])]});}
            var Q41;
            {var subQ0=sQuery(id+"F2.wireOp",EDGE,"E20.3.20.0");Q41=makeQuery(id+"F2.imprint","IMPRINT",FACE,{"disambiguationData":[TD([[makeQuery(id+"F2.imprint","IMPRINT",EDGE,{"derivedFrom":subQ0}),1.0]])]});}
            var Q42;
            {var subQ0=sQuery(id+"F2.wireOp",EDGE,"E20.9.21.0");Q42=makeQuery(id+"F2.imprint","IMPRINT",FACE,{"disambiguationData":[TD([[makeQuery(id+"F2.imprint","IMPRINT",EDGE,{"derivedFrom":subQ0}),-1.0]])]});}
            var Q43;
            {var subQ0=sQuery(id+"F2.wireOp",EDGE,"E20.3.21.0");Q43=makeQuery(id+"F2.imprint","IMPRINT",FACE,{"disambiguationData":[TD([[makeQuery(id+"F2.imprint","IMPRINT",EDGE,{"derivedFrom":subQ0}),1.0]])]});}
            var Q44;
            {var subQ0=sQuery(id+"F2.wireOp",EDGE,"E20.9.22.0");Q44=makeQuery(id+"F2.imprint","IMPRINT",FACE,{"disambiguationData":[TD([[makeQuery(id+"F2.imprint","IMPRINT",EDGE,{"derivedFrom":subQ0}),-1.0]])]});}
            var Q45;
            {var subQ0=sQuery(id+"F2.wireOp",EDGE,"E20.3.22.0");Q45=makeQuery(id+"F2.imprint","IMPRINT",FACE,{"disambiguationData":[TD([[makeQuery(id+"F2.imprint","IMPRINT",EDGE,{"derivedFrom":subQ0}),1.0]])]});}
            var Q46;
            {var subQ0=sQuery(id+"F2.wireOp",EDGE,"E20.9.23.0");Q46=makeQuery(id+"F2.imprint","IMPRINT",FACE,{"disambiguationData":[TD([[makeQuery(id+"F2.imprint","IMPRINT",EDGE,{"derivedFrom":subQ0}),-1.0]])]});}
            var Q47;
            {var subQ0=sQuery(id+"F2.wireOp",EDGE,"E20.3.23.0");Q47=makeQuery(id+"F2.imprint","IMPRINT",FACE,{"disambiguationData":[TD([[makeQuery(id+"F2.imprint","IMPRINT",EDGE,{"derivedFrom":subQ0}),1.0]])]});}
            var Q48;
            {var subQ0=sQuery(id+"F2.wireOp",EDGE,"E20.9.24.0");Q48=makeQuery(id+"F2.imprint","IMPRINT",FACE,{"disambiguationData":[TD([[makeQuery(id+"F2.imprint","IMPRINT",EDGE,{"derivedFrom":subQ0}),-1.0]])]});}
            var Q49;
            {var subQ0=sQuery(id+"F2.wireOp",EDGE,"E20.3.24.0");Q49=makeQuery(id+"F2.imprint","IMPRINT",FACE,{"disambiguationData":[TD([[makeQuery(id+"F2.imprint","IMPRINT",EDGE,{"derivedFrom":subQ0}),1.0]])]});}
            var Q50;
            {var subQ0=sQuery(id+"F2.wireOp",EDGE,"E20.9.25.0");Q50=makeQuery(id+"F2.imprint","IMPRINT",FACE,{"disambiguationData":[TD([[makeQuery(id+"F2.imprint","IMPRINT",EDGE,{"derivedFrom":subQ0}),-1.0]])]});}
            var Q51;
            {var subQ0=sQuery(id+"F2.wireOp",EDGE,"E20.3.25.0");Q51=makeQuery(id+"F2.imprint","IMPRINT",FACE,{"disambiguationData":[TD([[makeQuery(id+"F2.imprint","IMPRINT",EDGE,{"derivedFrom":subQ0}),1.0]])]});}
            var Q52;
            {var subQ0=sQuery(id+"F2.wireOp",EDGE,"E20.9.26.0");Q52=makeQuery(id+"F2.imprint","IMPRINT",FACE,{"disambiguationData":[TD([[makeQuery(id+"F2.imprint","IMPRINT",EDGE,{"derivedFrom":subQ0}),-1.0]])]});}
            var Q53;
            {var subQ0=sQuery(id+"F2.wireOp",EDGE,"E20.3.26.0");Q53=makeQuery(id+"F2.imprint","IMPRINT",FACE,{"disambiguationData":[TD([[makeQuery(id+"F2.imprint","IMPRINT",EDGE,{"derivedFrom":subQ0}),1.0]])]});}
            var Q54;
            {var subQ0=sQuery(id+"F2.wireOp",EDGE,"E20.9.27.0");Q54=makeQuery(id+"F2.imprint","IMPRINT",FACE,{"disambiguationData":[TD([[makeQuery(id+"F2.imprint","IMPRINT",EDGE,{"derivedFrom":subQ0}),-1.0]])]});}
            var Q55;
            {var subQ0=sQuery(id+"F2.wireOp",EDGE,"E20.3.27.0");Q55=makeQuery(id+"F2.imprint","IMPRINT",FACE,{"disambiguationData":[TD([[makeQuery(id+"F2.imprint","IMPRINT",EDGE,{"derivedFrom":subQ0}),1.0]])]});}
            var Q56;
            {var subQ0=sQuery(id+"F2.wireOp",EDGE,"E20.9.28.0");Q56=makeQuery(id+"F2.imprint","IMPRINT",FACE,{"disambiguationData":[TD([[makeQuery(id+"F2.imprint","IMPRINT",EDGE,{"derivedFrom":subQ0}),-1.0]])]});}
            var Q57;
            {var subQ0=sQuery(id+"F2.wireOp",EDGE,"E20.3.28.0");Q57=makeQuery(id+"F2.imprint","IMPRINT",FACE,{"disambiguationData":[TD([[makeQuery(id+"F2.imprint","IMPRINT",EDGE,{"derivedFrom":subQ0}),1.0]])]});}
            var Q58;
            {var subQ0=sQuery(id+"F2.wireOp",EDGE,"E20.9.29.0");Q58=makeQuery(id+"F2.imprint","IMPRINT",FACE,{"disambiguationData":[TD([[makeQuery(id+"F2.imprint","IMPRINT",EDGE,{"derivedFrom":subQ0}),-1.0]])]});}
            var Q59;
            {var subQ0=sQuery(id+"F2.wireOp",EDGE,"E20.3.29.0");Q59=makeQuery(id+"F2.imprint","IMPRINT",FACE,{"disambiguationData":[TD([[makeQuery(id+"F2.imprint","IMPRINT",EDGE,{"derivedFrom":subQ0}),1.0]])]});}
            var Q60;
            {var subQ0=sQuery(id+"F2.wireOp",EDGE,"E21.9.30.0");Q60=makeQuery(id+"F2.imprint","IMPRINT",FACE,{"disambiguationData":[TD([[makeQuery(id+"F2.imprint","IMPRINT",EDGE,{"derivedFrom":subQ0}),-1.0]])]});}
            var Q61;
            {var subQ0=sQuery(id+"F2.wireOp",EDGE,"E21.3.30.0");Q61=makeQuery(id+"F2.imprint","IMPRINT",FACE,{"disambiguationData":[TD([[makeQuery(id+"F2.imprint","IMPRINT",EDGE,{"derivedFrom":subQ0}),1.0]])]});}
            var Q62;
            {var subQ0=sQuery(id+"F2.wireOp",EDGE,"E21.9.31.0");Q62=makeQuery(id+"F2.imprint","IMPRINT",FACE,{"disambiguationData":[TD([[makeQuery(id+"F2.imprint","IMPRINT",EDGE,{"derivedFrom":subQ0}),-1.0]])]});}
            var Q63;
            {var subQ0=sQuery(id+"F2.wireOp",EDGE,"E21.3.31.0");Q63=makeQuery(id+"F2.imprint","IMPRINT",FACE,{"disambiguationData":[TD([[makeQuery(id+"F2.imprint","IMPRINT",EDGE,{"derivedFrom":subQ0}),1.0]])]});}
            var Q64;
            {var subQ0=sQuery(id+"F2.wireOp",EDGE,"E21.9.32.0");Q64=makeQuery(id+"F2.imprint","IMPRINT",FACE,{"disambiguationData":[TD([[makeQuery(id+"F2.imprint","IMPRINT",EDGE,{"derivedFrom":subQ0}),-1.0]])]});}
            var Q65;
            {var subQ0=sQuery(id+"F2.wireOp",EDGE,"E21.3.32.0");Q65=makeQuery(id+"F2.imprint","IMPRINT",FACE,{"disambiguationData":[TD([[makeQuery(id+"F2.imprint","IMPRINT",EDGE,{"derivedFrom":subQ0}),1.0]])]});}
            var Q66;
            {var subQ0=sQuery(id+"F2.wireOp",EDGE,"E21.9.33.0");Q66=makeQuery(id+"F2.imprint","IMPRINT",FACE,{"disambiguationData":[TD([[makeQuery(id+"F2.imprint","IMPRINT",EDGE,{"derivedFrom":subQ0}),-1.0]])]});}
            var Q67;
            {var subQ0=sQuery(id+"F2.wireOp",EDGE,"E21.3.33.0");Q67=makeQuery(id+"F2.imprint","IMPRINT",FACE,{"disambiguationData":[TD([[makeQuery(id+"F2.imprint","IMPRINT",EDGE,{"derivedFrom":subQ0}),1.0]])]});}
            var Q68;
            {var subQ0=sQuery(id+"F2.wireOp",EDGE,"E21.9.34.0");Q68=makeQuery(id+"F2.imprint","IMPRINT",FACE,{"disambiguationData":[TD([[makeQuery(id+"F2.imprint","IMPRINT",EDGE,{"derivedFrom":subQ0}),-1.0]])]});}
            var Q69;
            {var subQ0=sQuery(id+"F2.wireOp",EDGE,"E21.3.34.0");Q69=makeQuery(id+"F2.imprint","IMPRINT",FACE,{"disambiguationData":[TD([[makeQuery(id+"F2.imprint","IMPRINT",EDGE,{"derivedFrom":subQ0}),1.0]])]});}
            var Q70;
            {var subQ0=sQuery(id+"F2.wireOp",EDGE,"E21.3.35.0");Q70=makeQuery(id+"F2.imprint","IMPRINT",FACE,{"disambiguationData":[TD([[makeQuery(id+"F2.imprint","IMPRINT",EDGE,{"derivedFrom":subQ0}),1.0]])]});}
            var Q71;
            {var subQ0=sQuery(id+"F2.wireOp",EDGE,"E21.9.35.0");Q71=makeQuery(id+"F2.imprint","IMPRINT",FACE,{"disambiguationData":[TD([[makeQuery(id+"F2.imprint","IMPRINT",EDGE,{"derivedFrom":subQ0}),-1.0]])]});}
            var Q72;
            {var subQ0=sQuery(id+"F2.wireOp",EDGE,"E21.9.36.0");Q72=makeQuery(id+"F2.imprint","IMPRINT",FACE,{"disambiguationData":[TD([[makeQuery(id+"F2.imprint","IMPRINT",EDGE,{"derivedFrom":subQ0}),-1.0]])]});}
            var Q73;
            {var subQ0=sQuery(id+"F2.wireOp",EDGE,"E21.3.36.0");Q73=makeQuery(id+"F2.imprint","IMPRINT",FACE,{"disambiguationData":[TD([[makeQuery(id+"F2.imprint","IMPRINT",EDGE,{"derivedFrom":subQ0}),1.0]])]});}
            var Q74;
            {var subQ0=sQuery(id+"F2.wireOp",EDGE,"E21.9.37.0");Q74=makeQuery(id+"F2.imprint","IMPRINT",FACE,{"disambiguationData":[TD([[makeQuery(id+"F2.imprint","IMPRINT",EDGE,{"derivedFrom":subQ0}),-1.0]])]});}
            var Q75;
            {var subQ0=sQuery(id+"F2.wireOp",EDGE,"E21.3.37.0");Q75=makeQuery(id+"F2.imprint","IMPRINT",FACE,{"disambiguationData":[TD([[makeQuery(id+"F2.imprint","IMPRINT",EDGE,{"derivedFrom":subQ0}),1.0]])]});}
            var Q76;
            {var subQ0=sQuery(id+"F2.wireOp",EDGE,"E21.9.38.0");Q76=makeQuery(id+"F2.imprint","IMPRINT",FACE,{"disambiguationData":[TD([[makeQuery(id+"F2.imprint","IMPRINT",EDGE,{"derivedFrom":subQ0}),-1.0]])]});}
            var Q77;
            {var subQ0=sQuery(id+"F2.wireOp",EDGE,"E21.3.38.0");Q77=makeQuery(id+"F2.imprint","IMPRINT",FACE,{"disambiguationData":[TD([[makeQuery(id+"F2.imprint","IMPRINT",EDGE,{"derivedFrom":subQ0}),1.0]])]});}
            var Q78;
            {var subQ0=sQuery(id+"F2.wireOp",EDGE,"E21.9.39.0");Q78=makeQuery(id+"F2.imprint","IMPRINT",FACE,{"disambiguationData":[TD([[makeQuery(id+"F2.imprint","IMPRINT",EDGE,{"derivedFrom":subQ0}),-1.0]])]});}
            var Q79;
            {var subQ0=sQuery(id+"F2.wireOp",EDGE,"E21.3.39.0");Q79=makeQuery(id+"F2.imprint","IMPRINT",FACE,{"disambiguationData":[TD([[makeQuery(id+"F2.imprint","IMPRINT",EDGE,{"derivedFrom":subQ0}),1.0]])]});}
            var Q80;
            {var subQ0=sQuery(id+"F2.wireOp",EDGE,"E22.3.40.0");Q80=makeQuery(id+"F2.imprint","IMPRINT",FACE,{"disambiguationData":[TD([[makeQuery(id+"F2.imprint","IMPRINT",EDGE,{"derivedFrom":subQ0}),1.0]])]});}
            var Q81;
            {var subQ0=sQuery(id+"F2.wireOp",EDGE,"E22.3.41.0");Q81=makeQuery(id+"F2.imprint","IMPRINT",FACE,{"disambiguationData":[TD([[makeQuery(id+"F2.imprint","IMPRINT",EDGE,{"derivedFrom":subQ0}),1.0]])]});}
            var Q82;
            {var subQ0=sQuery(id+"F2.wireOp",EDGE,"E22.3.42.0");Q82=makeQuery(id+"F2.imprint","IMPRINT",FACE,{"disambiguationData":[TD([[makeQuery(id+"F2.imprint","IMPRINT",EDGE,{"derivedFrom":subQ0}),1.0]])]});}
            var Q83;
            {var subQ0=sQuery(id+"F2.wireOp",EDGE,"E22.9.42.0");Q83=makeQuery(id+"F2.imprint","IMPRINT",FACE,{"disambiguationData":[TD([[makeQuery(id+"F2.imprint","IMPRINT",EDGE,{"derivedFrom":subQ0}),-1.0]])]});}
            var Q84;
            {var subQ0=sQuery(id+"F2.wireOp",EDGE,"E22.9.41.0");Q84=makeQuery(id+"F2.imprint","IMPRINT",FACE,{"disambiguationData":[TD([[makeQuery(id+"F2.imprint","IMPRINT",EDGE,{"derivedFrom":subQ0}),-1.0]])]});}
            var Q85;
            {var subQ0=sQuery(id+"F2.wireOp",EDGE,"E22.9.40.0");Q85=makeQuery(id+"F2.imprint","IMPRINT",FACE,{"disambiguationData":[TD([[makeQuery(id+"F2.imprint","IMPRINT",EDGE,{"derivedFrom":subQ0}),-1.0]])]});}
            var Q86;
            Q86=makeQuery(id+"F1.opExtrude","SWEPT_FACE",FACE,{"disambiguationData":[OSD([sQuery(id+"F0.wireOp",EDGE,"E5.MirrorCS")])]});
            extrude(context, id + "F3", {"entities" : qUnion([Q0, Q1, Q2, Q3, Q4, Q5, Q6, Q7, Q8, Q9, Q10, Q11, Q12, Q13, Q14, Q15, Q16, Q17, Q18, Q19, Q20, Q21, Q22, Q23, Q24, Q25, Q26, Q27, Q28, Q29, Q30, Q31, Q32, Q33, Q34, Q35, Q36, Q37, Q38, Q39, Q40, Q41, Q42, Q43, Q44, Q45, Q46, Q47, Q48, Q49, Q50, Q51, Q52, Q53, Q54, Q55, Q56, Q57, Q58, Q59, Q60, Q61, Q62, Q63, Q64, Q65, Q66, Q67, Q68, Q69, Q70, Q71, Q72, Q73, Q74, Q75, Q76, Q77, Q78, Q79, Q80, Q81, Q82, Q83, Q84, Q85]), "operationType" : NewBodyOperationType.REMOVE, "endBound" : BoundingType.UP_TO_SURFACE, "oppositeDirection" : true, "endBoundEntityFace" : qUnion([Q86]), "depth" : 25.4 * mm});
        }
        {
            var Q0;
            Q0=makeQuery(id+"F0.imprint","IMPRINT",FACE,{"disambiguationData":[TD([[makeQuery(id+"F0.imprint","IMPRINT",EDGE,{"derivedFrom":sQuery(id+"F0.wireOp",EDGE,"E11.1.0.0")}),1.0]])]});
            extrude(context, id + "F4", {"entities" : qUnion([Q0]), "depth" : 349.25 * mm});
        }
        {
            var Q0;
            Q0=makeQuery(id+"F0.imprint","IMPRINT",FACE,{"disambiguationData":[TD([[makeQuery(id+"F0.imprint","IMPRINT",EDGE,{"derivedFrom":sQuery(id+"F0.wireOp",EDGE,"E11.2.0.0")}),1.0]])]});
            extrude(context, id + "F5", {"entities" : qUnion([Q0]), "depth" : 152.4 * mm});
        }
        {
            var Q0;
            Q0=makeQuery(id+"F4.opExtrude","SWEPT_FACE",FACE,{"disambiguationData":[OSD([sQuery(id+"F0.wireOp",EDGE,"E11.1.0.1")])]});
            var sketch = newSketch(context, id + "F6", { "sketchPlane" : qUnion([Q0])});
            skLineSegment(sketch, "E23.0", {"start": v(-33.43, 10.16) * mm, "end": v(-33.43, 52.41) * mm});
            skLineSegment(sketch, "E23.1", {"start": v(-38.13, 10.16) * mm, "end": v(-38.13, 52.41) * mm});
            skLineSegment(sketch, "E23.2", {"start": v(-89.74, 10.16) * mm, "end": v(-89.74, 52.41) * mm});
            skLineSegment(sketch, "E23.3", {"start": v(-283.29, 10.16) * mm, "end": v(-283.29, 52.41) * mm});
            skLineSegment(sketch, "E23.4", {"start": v(-270.38, 10.16) * mm, "end": v(-270.38, 52.41) * mm});
            skLineSegment(sketch, "E23.5", {"start": v(-322, 10.16) * mm, "end": v(-322, 52.41) * mm});
            skLineSegment(sketch, "E23.6", {"start": v(-63.93, 10.16) * mm, "end": v(-63.93, 52.41) * mm});
            skLineSegment(sketch, "E23.7", {"start": v(-46.33, 10.16) * mm, "end": v(-46.33, 52.41) * mm});
            skLineSegment(sketch, "E23.8", {"start": v(-291.5, 10.16) * mm, "end": v(-291.5, 52.41) * mm});
            skLineSegment(sketch, "E23.9", {"start": v(-296.19, 10.16) * mm, "end": v(-296.19, 52.41) * mm});
            skLineSegment(sketch, "E23.10", {"start": v(-141.35, 10.16) * mm, "end": v(-141.35, 52.41) * mm});
            skLineSegment(sketch, "E23.11", {"start": v(-192.96, 10.16) * mm, "end": v(-192.96, 52.41) * mm});
            skLineSegment(sketch, "E23.12", {"start": v(-244.58, 10.16) * mm, "end": v(-244.58, 52.41) * mm});
            skLineSegment(sketch, "E23.13", {"start": v(-20.52, 10.16) * mm, "end": v(-20.52, 52.41) * mm});
            skLineSegment(sketch, "E23.14", {"start": v(-278.59, 10.16) * mm, "end": v(-278.59, 52.41) * mm});
            skLineSegment(sketch, "E23.15", {"start": v(-330.2, 10.16) * mm, "end": v(-330.2, 52.41) * mm});
            skLineSegment(sketch, "E23.16", {"start": v(-25.22, 10.16) * mm, "end": v(-25.22, 52.41) * mm});
            skLineSegment(sketch, "E23.17", {"start": v(-72.14, 10.16) * mm, "end": v(-72.14, 52.41) * mm});
            skLineSegment(sketch, "E23.18", {"start": v(-123.75, 10.16) * mm, "end": v(-123.75, 52.41) * mm});
            skLineSegment(sketch, "E23.19", {"start": v(-175.36, 10.16) * mm, "end": v(-175.36, 52.41) * mm});
            skLineSegment(sketch, "E23.20", {"start": v(-226.97, 10.16) * mm, "end": v(-226.97, 52.41) * mm});
            skLineSegment(sketch, "E23.21", {"start": v(-12.32, 10.16) * mm, "end": v(-12.32, 52.41) * mm});
            skLineSegment(sketch, "E23.22", {"start": v(-180.06, 10.16) * mm, "end": v(-180.06, 52.41) * mm});
            skLineSegment(sketch, "E23.23", {"start": v(-231.67, 10.16) * mm, "end": v(-231.67, 52.41) * mm});
            skLineSegment(sketch, "E23.24", {"start": v(-76.83, 10.16) * mm, "end": v(-76.83, 52.41) * mm});
            skLineSegment(sketch, "E23.25", {"start": v(-128.45, 10.16) * mm, "end": v(-128.45, 52.41) * mm});
            skLineSegment(sketch, "E23.26", {"start": v(-7.62, 10.16) * mm, "end": v(-7.62, 52.41) * mm});
            skLineSegment(sketch, "E23.27", {"start": v(-265.68, 10.16) * mm, "end": v(-265.68, 52.41) * mm});
            skLineSegment(sketch, "E23.28", {"start": v(-317.3, 10.16) * mm, "end": v(-317.3, 52.41) * mm});
            skLineSegment(sketch, "E23.29", {"start": v(-51.03, 10.16) * mm, "end": v(-51.03, 52.41) * mm});
            skLineSegment(sketch, "E23.30", {"start": v(-214.07, 10.16) * mm, "end": v(-214.07, 52.41) * mm});
            skLineSegment(sketch, "E23.31", {"start": v(-162.46, 10.16) * mm, "end": v(-162.46, 52.41) * mm});
            skLineSegment(sketch, "E23.32", {"start": v(-59.23, 10.16) * mm, "end": v(-59.23, 52.41) * mm});
            skLineSegment(sketch, "E23.33", {"start": v(-110.85, 10.16) * mm, "end": v(-110.85, 52.41) * mm});
            skLineSegment(sketch, "E23.34", {"start": v(-167.16, 10.16) * mm, "end": v(-167.16, 52.41) * mm});
            skLineSegment(sketch, "E23.35", {"start": v(-218.77, 10.16) * mm, "end": v(-218.77, 52.41) * mm});
            skLineSegment(sketch, "E23.36", {"start": v(-115.54, 10.16) * mm, "end": v(-115.54, 52.41) * mm});
            skLineSegment(sketch, "E23.37", {"start": v(-304.4, 10.16) * mm, "end": v(-304.4, 52.41) * mm});
            skLineSegment(sketch, "E23.38", {"start": v(-97.94, 10.16) * mm, "end": v(-97.94, 52.41) * mm});
            skLineSegment(sketch, "E23.39", {"start": v(-239.88, 10.16) * mm, "end": v(-239.88, 52.41) * mm});
            skLineSegment(sketch, "E23.40", {"start": v(-188.26, 10.16) * mm, "end": v(-188.26, 52.41) * mm});
            skLineSegment(sketch, "E23.41", {"start": v(-136.65, 10.16) * mm, "end": v(-136.65, 52.41) * mm});
            skLineSegment(sketch, "E23.42", {"start": v(-85.04, 10.16) * mm, "end": v(-85.04, 52.41) * mm});
            skLineSegment(sketch, "E23.43", {"start": v(-102.64, 10.16) * mm, "end": v(-102.64, 52.41) * mm});
            skLineSegment(sketch, "E23.44", {"start": v(-257.48, 10.16) * mm, "end": v(-257.48, 52.41) * mm});
            skLineSegment(sketch, "E23.45", {"start": v(-205.87, 10.16) * mm, "end": v(-205.87, 52.41) * mm});
            skLineSegment(sketch, "E23.46", {"start": v(-154.25, 10.16) * mm, "end": v(-154.25, 52.41) * mm});
            skLineSegment(sketch, "E23.47", {"start": v(-309.1, 10.16) * mm, "end": v(-309.1, 52.41) * mm});
            skLineSegment(sketch, "E23.48", {"start": v(-201.17, 10.16) * mm, "end": v(-201.17, 52.41) * mm});
            skLineSegment(sketch, "E23.49", {"start": v(-252.78, 10.16) * mm, "end": v(-252.78, 52.41) * mm});
            skLineSegment(sketch, "E23.50", {"start": v(-149.56, 10.16) * mm, "end": v(-149.56, 52.41) * mm});
            skLineSegment(sketch, "E23.62", {"start": v(-89.74, 10.16) * mm, "end": v(-85.04, 10.16) * mm});
            skLineSegment(sketch, "E23.63", {"start": v(-141.35, 10.16) * mm, "end": v(-136.65, 10.16) * mm});
            skLineSegment(sketch, "E23.64", {"start": v(-192.96, 10.16) * mm, "end": v(-188.26, 10.16) * mm});
            skLineSegment(sketch, "E23.65", {"start": v(-244.58, 10.16) * mm, "end": v(-239.88, 10.16) * mm});
            skLineSegment(sketch, "E23.66", {"start": v(-38.13, 10.16) * mm, "end": v(-33.43, 10.16) * mm});
            skLineSegment(sketch, "E23.67", {"start": v(-334.9, 52.41) * mm, "end": v(-330.2, 52.41) * mm});
            skLineSegment(sketch, "E23.68", {"start": v(-38.13, 52.41) * mm, "end": v(-33.43, 52.41) * mm});
            skLineSegment(sketch, "E23.69", {"start": v(-12.32, 10.16) * mm, "end": v(-25.22, 10.16) * mm});
            skLineSegment(sketch, "E23.70", {"start": v(-63.93, 10.16) * mm, "end": v(-59.23, 10.16) * mm});
            skLineSegment(sketch, "E23.71", {"start": v(-309.1, 52.41) * mm, "end": v(-304.4, 52.41) * mm});
            skLineSegment(sketch, "E23.72", {"start": v(-51.03, 52.41) * mm, "end": v(-46.33, 52.41) * mm});
            skLineSegment(sketch, "E23.73", {"start": v(-102.64, 52.41) * mm, "end": v(-97.94, 52.41) * mm});
            skLineSegment(sketch, "E23.74", {"start": v(-141.35, 52.41) * mm, "end": v(-136.65, 52.41) * mm});
            skLineSegment(sketch, "E23.75", {"start": v(-244.58, 52.41) * mm, "end": v(-239.88, 52.41) * mm});
            skLineSegment(sketch, "E23.76", {"start": v(-192.96, 52.41) * mm, "end": v(-188.26, 52.41) * mm});
            skLineSegment(sketch, "E23.77", {"start": v(-89.74, 52.41) * mm, "end": v(-85.04, 52.41) * mm});
            skLineSegment(sketch, "E23.78", {"start": v(-283.29, 52.41) * mm, "end": v(-278.59, 52.41) * mm});
            skLineSegment(sketch, "E23.79", {"start": v(-25.22, 52.41) * mm, "end": v(-20.52, 52.41) * mm});
            skLineSegment(sketch, "E23.80", {"start": v(-76.84, 52.41) * mm, "end": v(-72.14, 52.41) * mm});
            skLineSegment(sketch, "E23.81", {"start": v(-180.06, 52.41) * mm, "end": v(-175.36, 52.41) * mm});
            skLineSegment(sketch, "E23.82", {"start": v(-128.45, 52.41) * mm, "end": v(-123.75, 52.41) * mm});
            skLineSegment(sketch, "E23.83", {"start": v(-231.67, 52.41) * mm, "end": v(-226.97, 52.41) * mm});
            skLineSegment(sketch, "E23.84", {"start": v(-25.22, 10.16) * mm, "end": v(-20.52, 10.16) * mm});
            skLineSegment(sketch, "E23.85", {"start": v(-283.29, 10.16) * mm, "end": v(-278.59, 10.16) * mm});
            skLineSegment(sketch, "E23.86", {"start": v(-12.32, 52.41) * mm, "end": v(-7.62, 52.41) * mm});
            skLineSegment(sketch, "E23.87", {"start": v(-76.84, 10.16) * mm, "end": v(-72.14, 10.16) * mm});
            skLineSegment(sketch, "E23.88", {"start": v(-180.06, 10.16) * mm, "end": v(-175.36, 10.16) * mm});
            skLineSegment(sketch, "E23.89", {"start": v(-128.45, 10.16) * mm, "end": v(-123.75, 10.16) * mm});
            skLineSegment(sketch, "E23.90", {"start": v(-231.67, 10.16) * mm, "end": v(-226.97, 10.16) * mm});
            skLineSegment(sketch, "E23.91", {"start": v(-12.32, 10.16) * mm, "end": v(-7.62, 10.16) * mm});
            skLineSegment(sketch, "E23.92", {"start": v(-270.38, 52.41) * mm, "end": v(-265.68, 52.41) * mm});
            skLineSegment(sketch, "E23.93", {"start": v(-322, 52.41) * mm, "end": v(-317.3, 52.41) * mm});
            skLineSegment(sketch, "E23.94", {"start": v(-167.16, 52.41) * mm, "end": v(-162.46, 52.41) * mm});
            skLineSegment(sketch, "E23.95", {"start": v(-218.77, 52.41) * mm, "end": v(-214.07, 52.41) * mm});
            skLineSegment(sketch, "E23.96", {"start": v(-115.54, 52.41) * mm, "end": v(-110.85, 52.41) * mm});
            skLineSegment(sketch, "E23.97", {"start": v(-63.93, 52.41) * mm, "end": v(-59.23, 52.41) * mm});
            skLineSegment(sketch, "E23.98", {"start": v(-51.03, 10.16) * mm, "end": v(-46.33, 10.16) * mm});
            skLineSegment(sketch, "E23.99", {"start": v(-270.38, 10.16) * mm, "end": v(-265.68, 10.16) * mm});
            skLineSegment(sketch, "E23.100", {"start": v(-322, 10.16) * mm, "end": v(-317.3, 10.16) * mm});
            skLineSegment(sketch, "E23.101", {"start": v(-167.16, 10.16) * mm, "end": v(-162.46, 10.16) * mm});
            skLineSegment(sketch, "E23.102", {"start": v(-218.77, 10.16) * mm, "end": v(-214.07, 10.16) * mm});
            skLineSegment(sketch, "E23.103", {"start": v(-154.25, 52.41) * mm, "end": v(-149.56, 52.41) * mm});
            skLineSegment(sketch, "E23.104", {"start": v(-257.48, 52.41) * mm, "end": v(-252.78, 52.41) * mm});
            skLineSegment(sketch, "E23.105", {"start": v(-205.87, 52.41) * mm, "end": v(-201.17, 52.41) * mm});
            skLineSegment(sketch, "E23.106", {"start": v(-115.54, 10.16) * mm, "end": v(-110.85, 10.16) * mm});
            skLineSegment(sketch, "E23.107", {"start": v(-296.19, 10.16) * mm, "end": v(-291.5, 10.16) * mm});
            skLineSegment(sketch, "E23.108", {"start": v(-296.19, 52.41) * mm, "end": v(-291.5, 52.41) * mm});
            skLineSegment(sketch, "E23.109", {"start": v(-102.64, 10.16) * mm, "end": v(-97.94, 10.16) * mm});
            skLineSegment(sketch, "E23.110", {"start": v(-257.48, 10.16) * mm, "end": v(-252.78, 10.16) * mm});
            skLineSegment(sketch, "E23.111", {"start": v(-205.87, 10.16) * mm, "end": v(-201.17, 10.16) * mm});
            skLineSegment(sketch, "E23.112", {"start": v(-154.25, 10.16) * mm, "end": v(-149.56, 10.16) * mm});
            skLineSegment(sketch, "E23.113", {"start": v(-309.1, 10.16) * mm, "end": v(-304.4, 10.16) * mm});
            skPoint(sketch, "E23.54.start.orphan", {"position": v(-152.4, 0) * mm});
            skPoint(sketch, "E24.orphan", {"position": v(-152.4, 1.9) * mm});
            skPoint(sketch, "E23.52.end.orphan", {"position": v(-152.4, 43.85) * mm});
            skPoint(sketch, "E25.orphan", {"position": v(-152.4, 52.41) * mm});
            skPoint(sketch, "E26.orphan", {"position": v(-152.4, 49.24) * mm});
            skPoint(sketch, "E23.114.end.orphan", {"position": v(-152.4, 44.45) * mm});
            skPoint(sketch, "E23.114.start.orphan", {"position": v(-152.4, 43.85) * mm});
            skPoint(sketch, "E23.56.end.orphan", {"position": v(-152.4, 50.3) * mm});
            skPoint(sketch, "E23.56.start.orphan", {"position": v(-152.4, 50) * mm});
            skSolve(sketch);
        }
        {
            var Q0;
            {var subQ0=sQuery(id+"F6.wireOp",EDGE,"E23.91");Q0=makeQuery(id+"F6.imprint","IMPRINT",FACE,{"disambiguationData":[TD([[makeQuery(id+"F6.imprint","IMPRINT",EDGE,{"derivedFrom":subQ0}),1.0]])]});}
            var Q1;
            {var subQ0=sQuery(id+"F6.wireOp",EDGE,"E23.86");Q1=makeQuery(id+"F6.imprint","IMPRINT",FACE,{"disambiguationData":[TD([[makeQuery(id+"F6.imprint","IMPRINT",EDGE,{"derivedFrom":subQ0}),-1.0]])]});}
            var Q2;
            {var subQ0=sQuery(id+"F6.wireOp",EDGE,"E23.79");Q2=makeQuery(id+"F6.imprint","IMPRINT",FACE,{"disambiguationData":[TD([[makeQuery(id+"F6.imprint","IMPRINT",EDGE,{"derivedFrom":subQ0}),-1.0]])]});}
            var Q3;
            {var subQ0=sQuery(id+"F6.wireOp",EDGE,"E23.84");Q3=makeQuery(id+"F6.imprint","IMPRINT",FACE,{"disambiguationData":[TD([[makeQuery(id+"F6.imprint","IMPRINT",EDGE,{"derivedFrom":subQ0}),1.0]])]});}
            var Q4;
            {var subQ0=sQuery(id+"F6.wireOp",EDGE,"E23.68");Q4=makeQuery(id+"F6.imprint","IMPRINT",FACE,{"disambiguationData":[TD([[makeQuery(id+"F6.imprint","IMPRINT",EDGE,{"derivedFrom":subQ0}),-1.0]])]});}
            var Q5;
            {var subQ0=sQuery(id+"F6.wireOp",EDGE,"E23.66");Q5=makeQuery(id+"F6.imprint","IMPRINT",FACE,{"disambiguationData":[TD([[makeQuery(id+"F6.imprint","IMPRINT",EDGE,{"derivedFrom":subQ0}),1.0]])]});}
            var Q6;
            {var subQ0=sQuery(id+"F6.wireOp",EDGE,"E23.72");Q6=makeQuery(id+"F6.imprint","IMPRINT",FACE,{"disambiguationData":[TD([[makeQuery(id+"F6.imprint","IMPRINT",EDGE,{"derivedFrom":subQ0}),-1.0]])]});}
            var Q7;
            {var subQ0=sQuery(id+"F6.wireOp",EDGE,"E23.98");Q7=makeQuery(id+"F6.imprint","IMPRINT",FACE,{"disambiguationData":[TD([[makeQuery(id+"F6.imprint","IMPRINT",EDGE,{"derivedFrom":subQ0}),1.0]])]});}
            var Q8;
            {var subQ0=sQuery(id+"F6.wireOp",EDGE,"E23.97");Q8=makeQuery(id+"F6.imprint","IMPRINT",FACE,{"disambiguationData":[TD([[makeQuery(id+"F6.imprint","IMPRINT",EDGE,{"derivedFrom":subQ0}),-1.0]])]});}
            var Q9;
            {var subQ0=sQuery(id+"F6.wireOp",EDGE,"E23.70");Q9=makeQuery(id+"F6.imprint","IMPRINT",FACE,{"disambiguationData":[TD([[makeQuery(id+"F6.imprint","IMPRINT",EDGE,{"derivedFrom":subQ0}),1.0]])]});}
            var Q10;
            {var subQ0=sQuery(id+"F6.wireOp",EDGE,"E23.80");Q10=makeQuery(id+"F6.imprint","IMPRINT",FACE,{"disambiguationData":[TD([[makeQuery(id+"F6.imprint","IMPRINT",EDGE,{"derivedFrom":subQ0}),-1.0]])]});}
            var Q11;
            {var subQ0=sQuery(id+"F6.wireOp",EDGE,"E23.87");Q11=makeQuery(id+"F6.imprint","IMPRINT",FACE,{"disambiguationData":[TD([[makeQuery(id+"F6.imprint","IMPRINT",EDGE,{"derivedFrom":subQ0}),1.0]])]});}
            var Q12;
            {var subQ0=sQuery(id+"F6.wireOp",EDGE,"E23.62");Q12=makeQuery(id+"F6.imprint","IMPRINT",FACE,{"disambiguationData":[TD([[makeQuery(id+"F6.imprint","IMPRINT",EDGE,{"derivedFrom":subQ0}),1.0]])]});}
            var Q13;
            {var subQ0=sQuery(id+"F6.wireOp",EDGE,"E23.73");Q13=makeQuery(id+"F6.imprint","IMPRINT",FACE,{"disambiguationData":[TD([[makeQuery(id+"F6.imprint","IMPRINT",EDGE,{"derivedFrom":subQ0}),-1.0]])]});}
            var Q14;
            {var subQ0=sQuery(id+"F6.wireOp",EDGE,"E23.109");Q14=makeQuery(id+"F6.imprint","IMPRINT",FACE,{"disambiguationData":[TD([[makeQuery(id+"F6.imprint","IMPRINT",EDGE,{"derivedFrom":subQ0}),1.0]])]});}
            var Q15;
            {var subQ0=sQuery(id+"F6.wireOp",EDGE,"E23.96");Q15=makeQuery(id+"F6.imprint","IMPRINT",FACE,{"disambiguationData":[TD([[makeQuery(id+"F6.imprint","IMPRINT",EDGE,{"derivedFrom":subQ0}),-1.0]])]});}
            var Q16;
            {var subQ0=sQuery(id+"F6.wireOp",EDGE,"E23.106");Q16=makeQuery(id+"F6.imprint","IMPRINT",FACE,{"disambiguationData":[TD([[makeQuery(id+"F6.imprint","IMPRINT",EDGE,{"derivedFrom":subQ0}),1.0]])]});}
            var Q17;
            {var subQ0=sQuery(id+"F6.wireOp",EDGE,"E23.82");Q17=makeQuery(id+"F6.imprint","IMPRINT",FACE,{"disambiguationData":[TD([[makeQuery(id+"F6.imprint","IMPRINT",EDGE,{"derivedFrom":subQ0}),-1.0]])]});}
            var Q18;
            {var subQ0=sQuery(id+"F6.wireOp",EDGE,"E23.89");Q18=makeQuery(id+"F6.imprint","IMPRINT",FACE,{"disambiguationData":[TD([[makeQuery(id+"F6.imprint","IMPRINT",EDGE,{"derivedFrom":subQ0}),1.0]])]});}
            var Q19;
            {var subQ0=sQuery(id+"F6.wireOp",EDGE,"E23.74");Q19=makeQuery(id+"F6.imprint","IMPRINT",FACE,{"disambiguationData":[TD([[makeQuery(id+"F6.imprint","IMPRINT",EDGE,{"derivedFrom":subQ0}),-1.0]])]});}
            var Q20;
            {var subQ0=sQuery(id+"F6.wireOp",EDGE,"E23.63");Q20=makeQuery(id+"F6.imprint","IMPRINT",FACE,{"disambiguationData":[TD([[makeQuery(id+"F6.imprint","IMPRINT",EDGE,{"derivedFrom":subQ0}),1.0]])]});}
            var Q21;
            {var subQ0=sQuery(id+"F6.wireOp",EDGE,"E23.103");Q21=makeQuery(id+"F6.imprint","IMPRINT",FACE,{"disambiguationData":[TD([[makeQuery(id+"F6.imprint","IMPRINT",EDGE,{"derivedFrom":subQ0}),-1.0]])]});}
            var Q22;
            {var subQ0=sQuery(id+"F6.wireOp",EDGE,"E23.112");Q22=makeQuery(id+"F6.imprint","IMPRINT",FACE,{"disambiguationData":[TD([[makeQuery(id+"F6.imprint","IMPRINT",EDGE,{"derivedFrom":subQ0}),1.0]])]});}
            var Q23;
            {var subQ0=sQuery(id+"F6.wireOp",EDGE,"E23.94");Q23=makeQuery(id+"F6.imprint","IMPRINT",FACE,{"disambiguationData":[TD([[makeQuery(id+"F6.imprint","IMPRINT",EDGE,{"derivedFrom":subQ0}),-1.0]])]});}
            var Q24;
            {var subQ0=sQuery(id+"F6.wireOp",EDGE,"E23.101");Q24=makeQuery(id+"F6.imprint","IMPRINT",FACE,{"disambiguationData":[TD([[makeQuery(id+"F6.imprint","IMPRINT",EDGE,{"derivedFrom":subQ0}),1.0]])]});}
            var Q25;
            {var subQ0=sQuery(id+"F6.wireOp",EDGE,"E23.81");Q25=makeQuery(id+"F6.imprint","IMPRINT",FACE,{"disambiguationData":[TD([[makeQuery(id+"F6.imprint","IMPRINT",EDGE,{"derivedFrom":subQ0}),-1.0]])]});}
            var Q26;
            {var subQ0=sQuery(id+"F6.wireOp",EDGE,"E23.88");Q26=makeQuery(id+"F6.imprint","IMPRINT",FACE,{"disambiguationData":[TD([[makeQuery(id+"F6.imprint","IMPRINT",EDGE,{"derivedFrom":subQ0}),1.0]])]});}
            var Q27;
            {var subQ0=sQuery(id+"F6.wireOp",EDGE,"E23.76");Q27=makeQuery(id+"F6.imprint","IMPRINT",FACE,{"disambiguationData":[TD([[makeQuery(id+"F6.imprint","IMPRINT",EDGE,{"derivedFrom":subQ0}),-1.0]])]});}
            var Q28;
            {var subQ0=sQuery(id+"F6.wireOp",EDGE,"E23.64");Q28=makeQuery(id+"F6.imprint","IMPRINT",FACE,{"disambiguationData":[TD([[makeQuery(id+"F6.imprint","IMPRINT",EDGE,{"derivedFrom":subQ0}),1.0]])]});}
            var Q29;
            {var subQ0=sQuery(id+"F6.wireOp",EDGE,"E23.105");Q29=makeQuery(id+"F6.imprint","IMPRINT",FACE,{"disambiguationData":[TD([[makeQuery(id+"F6.imprint","IMPRINT",EDGE,{"derivedFrom":subQ0}),-1.0]])]});}
            var Q30;
            {var subQ0=sQuery(id+"F6.wireOp",EDGE,"E23.111");Q30=makeQuery(id+"F6.imprint","IMPRINT",FACE,{"disambiguationData":[TD([[makeQuery(id+"F6.imprint","IMPRINT",EDGE,{"derivedFrom":subQ0}),1.0]])]});}
            var Q31;
            {var subQ0=sQuery(id+"F6.wireOp",EDGE,"E23.95");Q31=makeQuery(id+"F6.imprint","IMPRINT",FACE,{"disambiguationData":[TD([[makeQuery(id+"F6.imprint","IMPRINT",EDGE,{"derivedFrom":subQ0}),-1.0]])]});}
            var Q32;
            {var subQ0=sQuery(id+"F6.wireOp",EDGE,"E23.102");Q32=makeQuery(id+"F6.imprint","IMPRINT",FACE,{"disambiguationData":[TD([[makeQuery(id+"F6.imprint","IMPRINT",EDGE,{"derivedFrom":subQ0}),1.0]])]});}
            var Q33;
            {var subQ0=sQuery(id+"F6.wireOp",EDGE,"E23.83");Q33=makeQuery(id+"F6.imprint","IMPRINT",FACE,{"disambiguationData":[TD([[makeQuery(id+"F6.imprint","IMPRINT",EDGE,{"derivedFrom":subQ0}),-1.0]])]});}
            var Q34;
            {var subQ0=sQuery(id+"F6.wireOp",EDGE,"E23.90");Q34=makeQuery(id+"F6.imprint","IMPRINT",FACE,{"disambiguationData":[TD([[makeQuery(id+"F6.imprint","IMPRINT",EDGE,{"derivedFrom":subQ0}),1.0]])]});}
            var Q35;
            {var subQ0=sQuery(id+"F6.wireOp",EDGE,"E23.75");Q35=makeQuery(id+"F6.imprint","IMPRINT",FACE,{"disambiguationData":[TD([[makeQuery(id+"F6.imprint","IMPRINT",EDGE,{"derivedFrom":subQ0}),-1.0]])]});}
            var Q36;
            {var subQ0=sQuery(id+"F6.wireOp",EDGE,"E23.65");Q36=makeQuery(id+"F6.imprint","IMPRINT",FACE,{"disambiguationData":[TD([[makeQuery(id+"F6.imprint","IMPRINT",EDGE,{"derivedFrom":subQ0}),1.0]])]});}
            var Q37;
            {var subQ0=sQuery(id+"F6.wireOp",EDGE,"E23.104");Q37=makeQuery(id+"F6.imprint","IMPRINT",FACE,{"disambiguationData":[TD([[makeQuery(id+"F6.imprint","IMPRINT",EDGE,{"derivedFrom":subQ0}),-1.0]])]});}
            var Q38;
            {var subQ0=sQuery(id+"F6.wireOp",EDGE,"E23.110");Q38=makeQuery(id+"F6.imprint","IMPRINT",FACE,{"disambiguationData":[TD([[makeQuery(id+"F6.imprint","IMPRINT",EDGE,{"derivedFrom":subQ0}),1.0]])]});}
            var Q39;
            {var subQ0=sQuery(id+"F6.wireOp",EDGE,"E23.92");Q39=makeQuery(id+"F6.imprint","IMPRINT",FACE,{"disambiguationData":[TD([[makeQuery(id+"F6.imprint","IMPRINT",EDGE,{"derivedFrom":subQ0}),-1.0]])]});}
            var Q40;
            {var subQ0=sQuery(id+"F6.wireOp",EDGE,"E23.99");Q40=makeQuery(id+"F6.imprint","IMPRINT",FACE,{"disambiguationData":[TD([[makeQuery(id+"F6.imprint","IMPRINT",EDGE,{"derivedFrom":subQ0}),1.0]])]});}
            var Q41;
            {var subQ0=sQuery(id+"F6.wireOp",EDGE,"E23.78");Q41=makeQuery(id+"F6.imprint","IMPRINT",FACE,{"disambiguationData":[TD([[makeQuery(id+"F6.imprint","IMPRINT",EDGE,{"derivedFrom":subQ0}),-1.0]])]});}
            var Q42;
            {var subQ0=sQuery(id+"F6.wireOp",EDGE,"E23.85");Q42=makeQuery(id+"F6.imprint","IMPRINT",FACE,{"disambiguationData":[TD([[makeQuery(id+"F6.imprint","IMPRINT",EDGE,{"derivedFrom":subQ0}),1.0]])]});}
            var Q43;
            {var subQ0=sQuery(id+"F6.wireOp",EDGE,"E23.108");Q43=makeQuery(id+"F6.imprint","IMPRINT",FACE,{"disambiguationData":[TD([[makeQuery(id+"F6.imprint","IMPRINT",EDGE,{"derivedFrom":subQ0}),-1.0]])]});}
            var Q44;
            {var subQ0=sQuery(id+"F6.wireOp",EDGE,"E23.107");Q44=makeQuery(id+"F6.imprint","IMPRINT",FACE,{"disambiguationData":[TD([[makeQuery(id+"F6.imprint","IMPRINT",EDGE,{"derivedFrom":subQ0}),1.0]])]});}
            var Q45;
            {var subQ0=sQuery(id+"F6.wireOp",EDGE,"E23.71");Q45=makeQuery(id+"F6.imprint","IMPRINT",FACE,{"disambiguationData":[TD([[makeQuery(id+"F6.imprint","IMPRINT",EDGE,{"derivedFrom":subQ0}),-1.0]])]});}
            var Q46;
            {var subQ0=sQuery(id+"F6.wireOp",EDGE,"E23.113");Q46=makeQuery(id+"F6.imprint","IMPRINT",FACE,{"disambiguationData":[TD([[makeQuery(id+"F6.imprint","IMPRINT",EDGE,{"derivedFrom":subQ0}),1.0]])]});}
            var Q47;
            {var subQ0=sQuery(id+"F6.wireOp",EDGE,"E23.93");Q47=makeQuery(id+"F6.imprint","IMPRINT",FACE,{"disambiguationData":[TD([[makeQuery(id+"F6.imprint","IMPRINT",EDGE,{"derivedFrom":subQ0}),-1.0]])]});}
            var Q48;
            {var subQ0=sQuery(id+"F6.wireOp",EDGE,"E23.100");Q48=makeQuery(id+"F6.imprint","IMPRINT",FACE,{"disambiguationData":[TD([[makeQuery(id+"F6.imprint","IMPRINT",EDGE,{"derivedFrom":subQ0}),1.0]])]});}
            var Q49;
            {var subQ0=sQuery(id+"F6.wireOp",EDGE,"E23.77");Q49=makeQuery(id+"F6.imprint","IMPRINT",FACE,{"disambiguationData":[TD([[makeQuery(id+"F6.imprint","IMPRINT",EDGE,{"derivedFrom":subQ0}),-1.0]])]});}
            var Q50;
            Q50=makeQuery(id+"F4.opExtrude","SWEPT_FACE",FACE,{"disambiguationData":[OSD([sQuery(id+"F0.wireOp",EDGE,"E11.1.0.3")])]});
            extrude(context, id + "F7", {"entities" : qUnion([Q0, Q1, Q2, Q3, Q4, Q5, Q6, Q7, Q8, Q9, Q10, Q11, Q12, Q13, Q14, Q15, Q16, Q17, Q18, Q19, Q20, Q21, Q22, Q23, Q24, Q25, Q26, Q27, Q28, Q29, Q30, Q31, Q32, Q33, Q34, Q35, Q36, Q37, Q38, Q39, Q40, Q41, Q42, Q43, Q44, Q45, Q46, Q47, Q48, Q49]), "operationType" : NewBodyOperationType.REMOVE, "endBound" : BoundingType.UP_TO_SURFACE, "oppositeDirection" : true, "endBoundEntityFace" : qUnion([Q50]), "depth" : 25.4 * mm});
        }
        {
            var Q0;
            Q0=makeQuery(id+"F5.opExtrude","SWEPT_FACE",FACE,{"disambiguationData":[OSD([sQuery(id+"F0.wireOp",EDGE,"E11.2.0.1")])]});
            var sketch = newSketch(context, id + "F8", { "sketchPlane" : qUnion([Q0])});
            skLineSegment(sketch, "E27.0", {"start": v(-7.62, 10.16) * mm, "end": v(-7.62, 52.41) * mm});
            skLineSegment(sketch, "E27.1", {"start": v(-85.04, 10.16) * mm, "end": v(-85.04, 52.41) * mm});
            skLineSegment(sketch, "E27.2", {"start": v(-51.03, 10.16) * mm, "end": v(-51.03, 52.41) * mm});
            skLineSegment(sketch, "E27.3", {"start": v(-63.93, 10.16) * mm, "end": v(-63.93, 52.41) * mm});
            skLineSegment(sketch, "E27.4", {"start": v(-89.74, 10.16) * mm, "end": v(-89.74, 52.41) * mm});
            skLineSegment(sketch, "E27.5", {"start": v(-38.13, 10.16) * mm, "end": v(-38.13, 52.41) * mm});
            skLineSegment(sketch, "E27.6", {"start": v(-33.43, 10.16) * mm, "end": v(-33.43, 52.41) * mm});
            skLineSegment(sketch, "E27.7", {"start": v(-20.52, 10.16) * mm, "end": v(-20.52, 52.41) * mm});
            skLineSegment(sketch, "E27.8", {"start": v(-102.64, 10.16) * mm, "end": v(-102.64, 52.41) * mm});
            skLineSegment(sketch, "E27.9", {"start": v(-12.32, 10.16) * mm, "end": v(-25.22, 10.16) * mm});
            skLineSegment(sketch, "E27.10", {"start": v(-128.45, 10.16) * mm, "end": v(-128.45, 52.41) * mm});
            skLineSegment(sketch, "E27.11", {"start": v(-136.65, 10.16) * mm, "end": v(-136.65, 52.41) * mm});
            skLineSegment(sketch, "E27.12", {"start": v(-76.83, 10.16) * mm, "end": v(-76.83, 52.41) * mm});
            skLineSegment(sketch, "E27.13", {"start": v(-188.26, 10.16) * mm, "end": v(-188.26, 52.41) * mm});
            skLineSegment(sketch, "E27.14", {"start": v(-180.06, 10.16) * mm, "end": v(-180.06, 52.41) * mm});
            skLineSegment(sketch, "E27.15", {"start": v(-97.94, 10.16) * mm, "end": v(-97.94, 52.41) * mm});
            skLineSegment(sketch, "E27.16", {"start": v(-12.32, 10.16) * mm, "end": v(-12.32, 52.41) * mm});
            skLineSegment(sketch, "E27.17", {"start": v(-115.54, 10.16) * mm, "end": v(-115.54, 52.41) * mm});
            skLineSegment(sketch, "E27.18", {"start": v(-123.75, 10.16) * mm, "end": v(-123.75, 52.41) * mm});
            skLineSegment(sketch, "E27.19", {"start": v(-167.16, 10.16) * mm, "end": v(-167.16, 52.41) * mm});
            skLineSegment(sketch, "E27.20", {"start": v(-149.56, 10.16) * mm, "end": v(-149.56, 52.41) * mm});
            skLineSegment(sketch, "E27.21", {"start": v(-72.14, 10.16) * mm, "end": v(-72.14, 52.41) * mm});
            skLineSegment(sketch, "E27.22", {"start": v(-110.85, 10.16) * mm, "end": v(-110.85, 52.41) * mm});
            skLineSegment(sketch, "E27.23", {"start": v(-25.22, 10.16) * mm, "end": v(-25.22, 52.41) * mm});
            skLineSegment(sketch, "E27.24", {"start": v(-59.23, 10.16) * mm, "end": v(-59.23, 52.41) * mm});
            skLineSegment(sketch, "E27.25", {"start": v(-162.46, 10.16) * mm, "end": v(-162.46, 52.41) * mm});
            skLineSegment(sketch, "E27.26", {"start": v(-154.25, 10.16) * mm, "end": v(-154.25, 52.41) * mm});
            skLineSegment(sketch, "E27.27", {"start": v(-141.35, 10.16) * mm, "end": v(-141.35, 52.41) * mm});
            skLineSegment(sketch, "E27.28", {"start": v(-46.33, 10.16) * mm, "end": v(-46.33, 52.41) * mm});
            skLineSegment(sketch, "E27.29", {"start": v(-175.36, 10.16) * mm, "end": v(-175.36, 52.41) * mm});
            skLineSegment(sketch, "E27.30", {"start": v(-63.93, 10.16) * mm, "end": v(-59.23, 10.16) * mm});
            skLineSegment(sketch, "E27.31", {"start": v(-12.32, 52.41) * mm, "end": v(-7.62, 52.41) * mm});
            skLineSegment(sketch, "E27.32", {"start": v(-38.13, 52.41) * mm, "end": v(-33.43, 52.41) * mm});
            skLineSegment(sketch, "E27.33", {"start": v(-25.22, 10.16) * mm, "end": v(-20.52, 10.16) * mm});
            skLineSegment(sketch, "E27.34", {"start": v(-89.74, 10.16) * mm, "end": v(-85.04, 10.16) * mm});
            skLineSegment(sketch, "E27.35", {"start": v(-102.64, 10.16) * mm, "end": v(-97.94, 10.16) * mm});
            skLineSegment(sketch, "E27.36", {"start": v(-12.32, 10.16) * mm, "end": v(-7.62, 10.16) * mm});
            skLineSegment(sketch, "E27.37", {"start": v(-180.06, 10.16) * mm, "end": v(-175.36, 10.16) * mm});
            skLineSegment(sketch, "E27.38", {"start": v(-76.84, 10.16) * mm, "end": v(-72.14, 10.16) * mm});
            skLineSegment(sketch, "E27.39", {"start": v(-154.25, 52.41) * mm, "end": v(-149.56, 52.41) * mm});
            skLineSegment(sketch, "E27.40", {"start": v(-167.16, 10.16) * mm, "end": v(-162.46, 10.16) * mm});
            skLineSegment(sketch, "E27.41", {"start": v(-128.45, 52.41) * mm, "end": v(-123.75, 52.41) * mm});
            skLineSegment(sketch, "E27.42", {"start": v(-38.13, 10.16) * mm, "end": v(-33.43, 10.16) * mm});
            skLineSegment(sketch, "E27.43", {"start": v(-51.03, 10.16) * mm, "end": v(-46.33, 10.16) * mm});
            skLineSegment(sketch, "E27.44", {"start": v(-63.93, 52.41) * mm, "end": v(-59.23, 52.41) * mm});
            skLineSegment(sketch, "E27.45", {"start": v(-115.54, 52.41) * mm, "end": v(-110.85, 52.41) * mm});
            skLineSegment(sketch, "E27.46", {"start": v(-154.25, 10.16) * mm, "end": v(-149.56, 10.16) * mm});
            skLineSegment(sketch, "E27.47", {"start": v(-76.84, 52.41) * mm, "end": v(-72.14, 52.41) * mm});
            skLineSegment(sketch, "E27.48", {"start": v(-25.22, 52.41) * mm, "end": v(-20.52, 52.41) * mm});
            skLineSegment(sketch, "E27.49", {"start": v(-141.35, 10.16) * mm, "end": v(-136.65, 10.16) * mm});
            skLineSegment(sketch, "E27.50", {"start": v(-167.16, 52.41) * mm, "end": v(-162.46, 52.41) * mm});
            skLineSegment(sketch, "E27.51", {"start": v(-89.74, 52.41) * mm, "end": v(-85.04, 52.41) * mm});
            skLineSegment(sketch, "E27.52", {"start": v(-141.35, 52.41) * mm, "end": v(-136.65, 52.41) * mm});
            skLineSegment(sketch, "E27.53", {"start": v(-128.45, 10.16) * mm, "end": v(-123.75, 10.16) * mm});
            skLineSegment(sketch, "E27.54", {"start": v(-102.64, 52.41) * mm, "end": v(-97.94, 52.41) * mm});
            skLineSegment(sketch, "E27.55", {"start": v(-51.03, 52.41) * mm, "end": v(-46.33, 52.41) * mm});
            skLineSegment(sketch, "E27.56", {"start": v(-115.54, 10.16) * mm, "end": v(-110.85, 10.16) * mm});
            skLineSegment(sketch, "E27.57", {"start": v(-180.06, 52.41) * mm, "end": v(-175.36, 52.41) * mm});
            skLineSegment(sketch, "E27.58", {"start": v(-152.4, 44.45) * mm, "end": v(-152.4, 49.24) * mm});
            skLineSegment(sketch, "E27.59", {"start": v(-152.4, 50.3) * mm, "end": v(-152.4, 52.41) * mm});
            skLineSegment(sketch, "E27.60", {"start": v(-152.4, 43.85) * mm, "end": v(-152.4, 50) * mm});
            skLineSegment(sketch, "E27.61", {"start": v(-152.4, 49.24) * mm, "end": v(-152.4, 50.3) * mm});
            skLineSegment(sketch, "E27.62", {"start": v(-152.4, 43.85) * mm, "end": v(-152.4, 50) * mm});
            skLineSegment(sketch, "E27.63", {"start": v(-152.4, 50) * mm, "end": v(-152.4, 52.41) * mm});
            skLineSegment(sketch, "E27.64", {"start": v(-152.4, 50) * mm, "end": v(-152.4, 52.41) * mm});
            skLineSegment(sketch, "E27.65", {"start": v(-152.4, 44.45) * mm, "end": v(-152.4, 49.24) * mm});
            skLineSegment(sketch, "E27.66", {"start": v(-152.4, 50.3) * mm, "end": v(-152.4, 52.41) * mm});
            skLineSegment(sketch, "E27.67", {"start": v(-152.4, 49.24) * mm, "end": v(-152.4, 50.3) * mm});
            skSolve(sketch);
        }
        {
            var Q0;
            {var subQ0=sQuery(id+"F8.wireOp",EDGE,"E27.36");Q0=makeQuery(id+"F8.imprint","IMPRINT",FACE,{"disambiguationData":[TD([[makeQuery(id+"F8.imprint","IMPRINT",EDGE,{"derivedFrom":subQ0}),1.0]])]});}
            var Q1;
            {var subQ0=sQuery(id+"F8.wireOp",EDGE,"E27.31");Q1=makeQuery(id+"F8.imprint","IMPRINT",FACE,{"disambiguationData":[TD([[makeQuery(id+"F8.imprint","IMPRINT",EDGE,{"derivedFrom":subQ0}),-1.0]])]});}
            var Q2;
            {var subQ0=sQuery(id+"F8.wireOp",EDGE,"E27.48");Q2=makeQuery(id+"F8.imprint","IMPRINT",FACE,{"disambiguationData":[TD([[makeQuery(id+"F8.imprint","IMPRINT",EDGE,{"derivedFrom":subQ0}),-1.0]])]});}
            var Q3;
            {var subQ0=sQuery(id+"F8.wireOp",EDGE,"E27.33");Q3=makeQuery(id+"F8.imprint","IMPRINT",FACE,{"disambiguationData":[TD([[makeQuery(id+"F8.imprint","IMPRINT",EDGE,{"derivedFrom":subQ0}),1.0]])]});}
            var Q4;
            {var subQ0=sQuery(id+"F8.wireOp",EDGE,"E27.32");Q4=makeQuery(id+"F8.imprint","IMPRINT",FACE,{"disambiguationData":[TD([[makeQuery(id+"F8.imprint","IMPRINT",EDGE,{"derivedFrom":subQ0}),-1.0]])]});}
            var Q5;
            {var subQ0=sQuery(id+"F8.wireOp",EDGE,"E27.42");Q5=makeQuery(id+"F8.imprint","IMPRINT",FACE,{"disambiguationData":[TD([[makeQuery(id+"F8.imprint","IMPRINT",EDGE,{"derivedFrom":subQ0}),1.0]])]});}
            var Q6;
            {var subQ0=sQuery(id+"F8.wireOp",EDGE,"E27.55");Q6=makeQuery(id+"F8.imprint","IMPRINT",FACE,{"disambiguationData":[TD([[makeQuery(id+"F8.imprint","IMPRINT",EDGE,{"derivedFrom":subQ0}),-1.0]])]});}
            var Q7;
            {var subQ0=sQuery(id+"F8.wireOp",EDGE,"E27.43");Q7=makeQuery(id+"F8.imprint","IMPRINT",FACE,{"disambiguationData":[TD([[makeQuery(id+"F8.imprint","IMPRINT",EDGE,{"derivedFrom":subQ0}),1.0]])]});}
            var Q8;
            {var subQ0=sQuery(id+"F8.wireOp",EDGE,"E27.44");Q8=makeQuery(id+"F8.imprint","IMPRINT",FACE,{"disambiguationData":[TD([[makeQuery(id+"F8.imprint","IMPRINT",EDGE,{"derivedFrom":subQ0}),-1.0]])]});}
            var Q9;
            {var subQ0=sQuery(id+"F8.wireOp",EDGE,"E27.30");Q9=makeQuery(id+"F8.imprint","IMPRINT",FACE,{"disambiguationData":[TD([[makeQuery(id+"F8.imprint","IMPRINT",EDGE,{"derivedFrom":subQ0}),1.0]])]});}
            var Q10;
            {var subQ0=sQuery(id+"F8.wireOp",EDGE,"E27.47");Q10=makeQuery(id+"F8.imprint","IMPRINT",FACE,{"disambiguationData":[TD([[makeQuery(id+"F8.imprint","IMPRINT",EDGE,{"derivedFrom":subQ0}),-1.0]])]});}
            var Q11;
            {var subQ0=sQuery(id+"F8.wireOp",EDGE,"E27.38");Q11=makeQuery(id+"F8.imprint","IMPRINT",FACE,{"disambiguationData":[TD([[makeQuery(id+"F8.imprint","IMPRINT",EDGE,{"derivedFrom":subQ0}),1.0]])]});}
            var Q12;
            {var subQ0=sQuery(id+"F8.wireOp",EDGE,"E27.51");Q12=makeQuery(id+"F8.imprint","IMPRINT",FACE,{"disambiguationData":[TD([[makeQuery(id+"F8.imprint","IMPRINT",EDGE,{"derivedFrom":subQ0}),-1.0]])]});}
            var Q13;
            {var subQ0=sQuery(id+"F8.wireOp",EDGE,"E27.34");Q13=makeQuery(id+"F8.imprint","IMPRINT",FACE,{"disambiguationData":[TD([[makeQuery(id+"F8.imprint","IMPRINT",EDGE,{"derivedFrom":subQ0}),1.0]])]});}
            var Q14;
            {var subQ0=sQuery(id+"F8.wireOp",EDGE,"E27.54");Q14=makeQuery(id+"F8.imprint","IMPRINT",FACE,{"disambiguationData":[TD([[makeQuery(id+"F8.imprint","IMPRINT",EDGE,{"derivedFrom":subQ0}),-1.0]])]});}
            var Q15;
            {var subQ0=sQuery(id+"F8.wireOp",EDGE,"E27.35");Q15=makeQuery(id+"F8.imprint","IMPRINT",FACE,{"disambiguationData":[TD([[makeQuery(id+"F8.imprint","IMPRINT",EDGE,{"derivedFrom":subQ0}),1.0]])]});}
            var Q16;
            {var subQ0=sQuery(id+"F8.wireOp",EDGE,"E27.45");Q16=makeQuery(id+"F8.imprint","IMPRINT",FACE,{"disambiguationData":[TD([[makeQuery(id+"F8.imprint","IMPRINT",EDGE,{"derivedFrom":subQ0}),-1.0]])]});}
            var Q17;
            {var subQ0=sQuery(id+"F8.wireOp",EDGE,"E27.56");Q17=makeQuery(id+"F8.imprint","IMPRINT",FACE,{"disambiguationData":[TD([[makeQuery(id+"F8.imprint","IMPRINT",EDGE,{"derivedFrom":subQ0}),1.0]])]});}
            var Q18;
            {var subQ0=sQuery(id+"F8.wireOp",EDGE,"E27.41");Q18=makeQuery(id+"F8.imprint","IMPRINT",FACE,{"disambiguationData":[TD([[makeQuery(id+"F8.imprint","IMPRINT",EDGE,{"derivedFrom":subQ0}),-1.0]])]});}
            var Q19;
            {var subQ0=sQuery(id+"F8.wireOp",EDGE,"E27.53");Q19=makeQuery(id+"F8.imprint","IMPRINT",FACE,{"disambiguationData":[TD([[makeQuery(id+"F8.imprint","IMPRINT",EDGE,{"derivedFrom":subQ0}),1.0]])]});}
            var Q20;
            {var subQ0=sQuery(id+"F8.wireOp",EDGE,"E27.52");Q20=makeQuery(id+"F8.imprint","IMPRINT",FACE,{"disambiguationData":[TD([[makeQuery(id+"F8.imprint","IMPRINT",EDGE,{"derivedFrom":subQ0}),-1.0]])]});}
            var Q21;
            {var subQ0=sQuery(id+"F8.wireOp",EDGE,"E27.49");Q21=makeQuery(id+"F8.imprint","IMPRINT",FACE,{"disambiguationData":[TD([[makeQuery(id+"F8.imprint","IMPRINT",EDGE,{"derivedFrom":subQ0}),1.0]])]});}
            var Q22;
            {var subQ0=sQuery(id+"F8.wireOp",EDGE,"E27.39");Q22=makeQuery(id+"F8.imprint","IMPRINT",FACE,{"disambiguationData":[TD([[makeQuery(id+"F8.imprint","IMPRINT",EDGE,{"derivedFrom":subQ0}),-1.0]])]});}
            var Q23;
            {var subQ0=sQuery(id+"F8.wireOp",EDGE,"E27.46");Q23=makeQuery(id+"F8.imprint","IMPRINT",FACE,{"disambiguationData":[TD([[makeQuery(id+"F8.imprint","IMPRINT",EDGE,{"derivedFrom":subQ0}),1.0]])]});}
            var Q24;
            {var subQ0=sQuery(id+"F8.wireOp",EDGE,"E27.50");Q24=makeQuery(id+"F8.imprint","IMPRINT",FACE,{"disambiguationData":[TD([[makeQuery(id+"F8.imprint","IMPRINT",EDGE,{"derivedFrom":subQ0}),-1.0]])]});}
            var Q25;
            {var subQ0=sQuery(id+"F8.wireOp",EDGE,"E27.40");Q25=makeQuery(id+"F8.imprint","IMPRINT",FACE,{"disambiguationData":[TD([[makeQuery(id+"F8.imprint","IMPRINT",EDGE,{"derivedFrom":subQ0}),1.0]])]});}
            var Q26;
            Q26=makeQuery(id+"F5.opExtrude","SWEPT_FACE",FACE,{"disambiguationData":[OSD([sQuery(id+"F0.wireOp",EDGE,"E11.2.0.3")])]});
            extrude(context, id + "F9", {"entities" : qUnion([Q0, Q1, Q2, Q3, Q4, Q5, Q6, Q7, Q8, Q9, Q10, Q11, Q12, Q13, Q14, Q15, Q16, Q17, Q18, Q19, Q20, Q21, Q22, Q23, Q24, Q25]), "operationType" : NewBodyOperationType.REMOVE, "endBound" : BoundingType.UP_TO_SURFACE, "oppositeDirection" : true, "endBoundEntityFace" : qUnion([Q26]), "depth" : 25.4 * mm});
        }
    });
